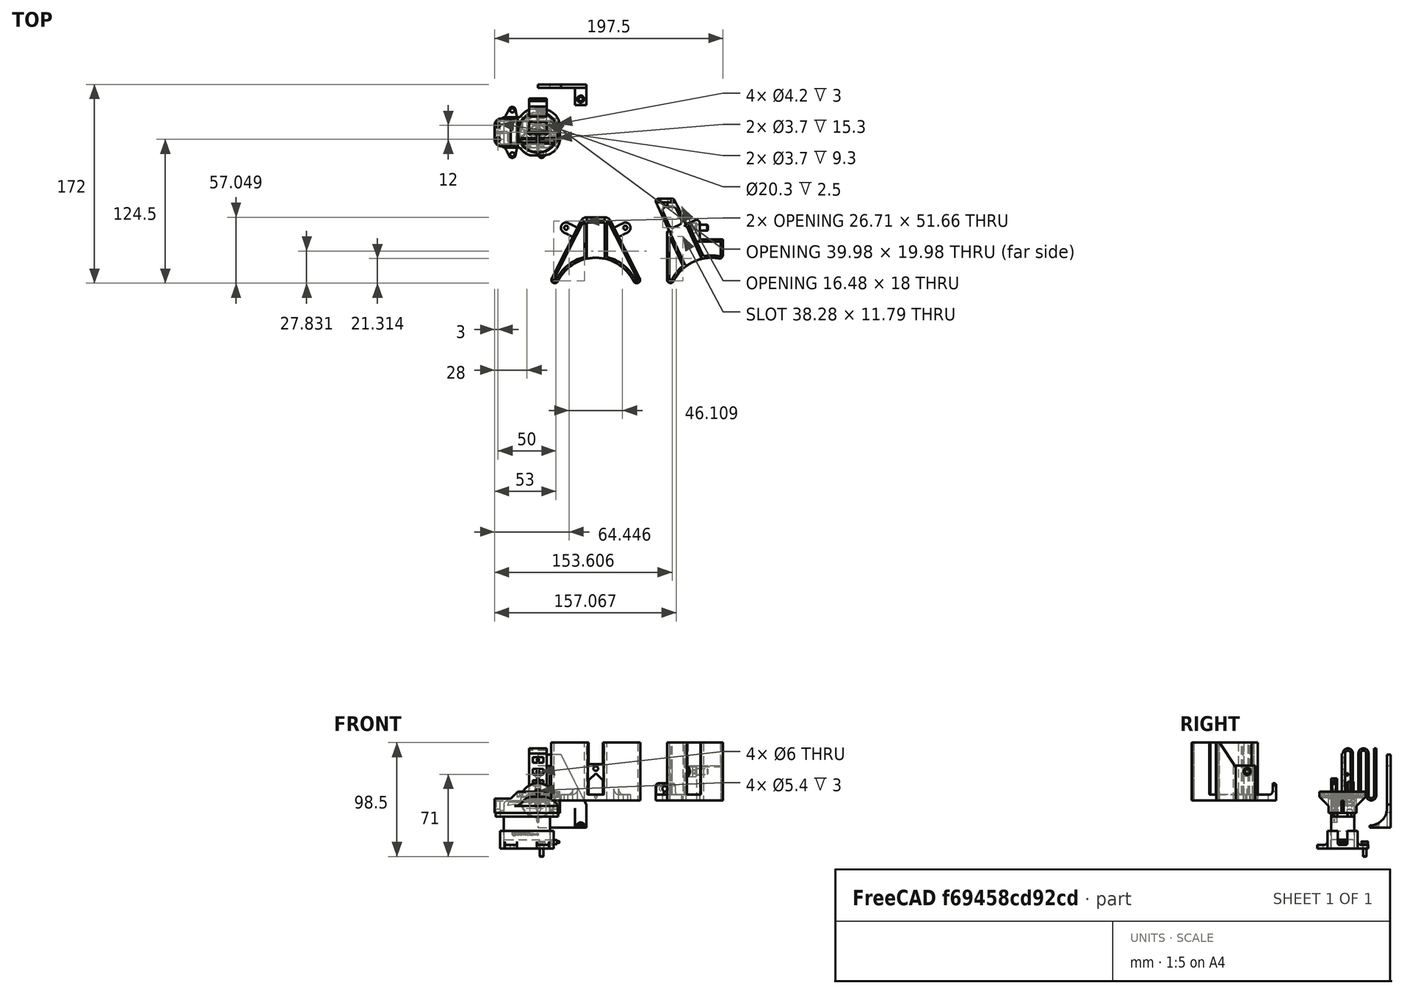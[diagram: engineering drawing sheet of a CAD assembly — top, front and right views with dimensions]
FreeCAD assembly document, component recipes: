
FREECAD ASSEMBLY — COMPONENT RECIPES ("OuterCanMover")

This assembly document has 7 components, labeled P0..P6 below (a component is one placed body or linked part). 7 of them carry a construction recipe — the FreeCAD feature program that regenerates the part from scratch, quoted from this document or its linked companion documents; the rest are supplied as boundary geometry only. No exploded tour is included for this assembly.
COMPONENT P0 — recipe-attached ("aimant", modeled in this document).
Construction recipe (the document's own serialized feature program — sketch geometry with constraints, then the solid features built on it; lengths are millimeters unless a unit is written):

FEATURE [Sketcher::SketchObject] Sketch004
  ArcFitTolerance = 1e-06
  AttachmentSupport = -> [XY_Plane003]
  FullyConstrained = true
  MakeInternals = false
  MapMode = 5
  sketch-geometry (4):
    g0: LineSegment StartX=4.5 StartY=-2.25 StartZ=0 EndX=4.5 EndY=2.25 EndZ=0
    g1: LineSegment StartX=4.5 StartY=2.25 StartZ=0 EndX=-4.5 EndY=2.25 EndZ=0
    g2: LineSegment StartX=-4.5 StartY=2.25 StartZ=0 EndX=-4.5 EndY=-2.25 EndZ=0
    g3: LineSegment StartX=-4.5 StartY=-2.25 StartZ=0 EndX=4.5 EndY=-2.25 EndZ=0
  constraints (11):
    c: Coincident(g0,g1)
    c: Coincident(g1,g2)
    c: Coincident(g2,g3)
    c: Coincident(g3,g0)
    c: Vertical(g0)
    c: Vertical(g2)
    c: Horizontal(g1)
    c: Horizontal(g3)
    c: Symmetric(g1,g0,g-1)
    c: DistanceX(g1,g1) = 9
    c: Distance(g2,g2) = 4.5
FEATURE [PartDesign::Pad] Pad002
  Direction = (0,0,1)
  Length = 2.5
  Length2 = 10
  Profile = -> Sketch004
  ReferenceAxis = -> Sketch004 [N_Axis]
  Suppressed = false
  Type = 0
FEATURE [PartDesign::Body] Body002  label="aimant"
  AllowCompound = false
  Group = -> [Sketch004,Pad002]
  Origin = -> Origin003
  Tip = -> Pad002
COMPONENT P1 — recipe-attached ("aimant002", modeled in this document).
Construction recipe (the document's own serialized feature program — sketch geometry with constraints, then the solid features built on it; lengths are millimeters unless a unit is written):

FEATURE [Sketcher::SketchObject] Sketch032
  ArcFitTolerance = 1e-06
  AttachmentSupport = -> [XY_Plane014]
  FullyConstrained = true
  MakeInternals = false
  MapMode = 5
  sketch-geometry (4):
    g0: LineSegment StartX=4.5 StartY=-2.25 StartZ=0 EndX=4.5 EndY=2.25 EndZ=0
    g1: LineSegment StartX=4.5 StartY=2.25 StartZ=0 EndX=-4.5 EndY=2.25 EndZ=0
    g2: LineSegment StartX=-4.5 StartY=2.25 StartZ=0 EndX=-4.5 EndY=-2.25 EndZ=0
    g3: LineSegment StartX=-4.5 StartY=-2.25 StartZ=0 EndX=4.5 EndY=-2.25 EndZ=0
  constraints (11):
    c: Coincident(g0,g1)
    c: Coincident(g1,g2)
    c: Coincident(g2,g3)
    c: Coincident(g3,g0)
    c: Vertical(g0)
    c: Vertical(g2)
    c: Horizontal(g1)
    c: Horizontal(g3)
    c: Symmetric(g1,g0,g-1)
    c: DistanceX(g1,g1) = 9
    c: Distance(g2,g2) = 4.5
FEATURE [PartDesign::Pad] Pad014
  Direction = (0,0,1)
  Length = 2.5
  Length2 = 10
  Profile = -> Sketch032
  ReferenceAxis = -> Sketch032 [N_Axis]
  Suppressed = false
  Type = 0
FEATURE [PartDesign::Body] Body008  label="aimant002"
  AllowCompound = false
  Group = -> [Sketch032,Pad014]
  Origin = -> Origin014
  Tip = -> Pad014
COMPONENT P2 — recipe-attached ("OuterCanMover_G", modeled in this document).
Construction recipe (the document's own serialized feature program — sketch geometry with constraints, then the solid features built on it; lengths are millimeters unless a unit is written):

FEATURE [Sketcher::SketchObject] Sketch
  ArcFitTolerance = 1e-06
  AttachmentSupport = -> [XY_Plane]
  FullyConstrained = true
  MakeInternals = false
  MapMode = 5
  sketch-geometry (18):
    g0: Circle [constr] CenterX=0 CenterY=-62.5 CenterZ=0 NormalX=0 NormalY=0 NormalZ=1 AngleXU=0 Radius=36.25
    g1: LineSegment [constr] StartX=-10 StartY=10 StartZ=0 EndX=-10 EndY=-10 EndZ=0
    g2: LineSegment [constr] StartX=-10 StartY=-10 StartZ=0 EndX=10 EndY=-10 EndZ=0
    g3: LineSegment [constr] StartX=10 StartY=-10 StartZ=0 EndX=10 EndY=10 EndZ=0
    g4: LineSegment [constr] StartX=10 StartY=10 StartZ=0 EndX=-10 EndY=10 EndZ=0
    g5: ArcOfCircle CenterX=0 CenterY=-62.5 CenterZ=0 NormalX=0 NormalY=0 NormalZ=1 AngleXU=0 Radius=36.5 StartAngle=1.39264 EndAngle=2.6779
    g6: LineSegment StartX=10 StartY=-10 StartZ=0 EndX=-10 EndY=-10 EndZ=0
    g7: LineSegment StartX=-10 StartY=-10 StartZ=0 EndX=-10 EndY=10 EndZ=0
    g8: LineSegment StartX=-14 StartY=14 StartZ=0 EndX=-23.3291 EndY=14 EndZ=0
    g9: LineSegment StartX=-38.3291 StartY=-1 StartZ=0 EndX=-38.3291 EndY=-44.8335 EndZ=0
    g10: ArcOfCircle CenterX=-14 CenterY=10 CenterZ=0 NormalX=0 NormalY=0 NormalZ=1 AngleXU=0 Radius=4 StartAngle=0 EndAngle=1.5708
    g11: GeomPoint [constr] X=-10 Y=14 Z=0
    g12: LineSegment StartX=10 StartY=-10 StartZ=0 EndX=10 EndY=-23.6252 EndZ=0
    g13: ArcOfCircle CenterX=-35.3291 CenterY=-44.8335 CenterZ=0 NormalX=0 NormalY=0 NormalZ=1 AngleXU=0 Radius=3 StartAngle=3.14159 EndAngle=5.81949
    g14: ArcOfCircle CenterX=7 CenterY=-23.6252 CenterZ=0 NormalX=0 NormalY=0 NormalZ=1 AngleXU=0 Radius=3 StartAngle=4.53423 EndAngle=6.28319
    g15: LineSegment [constr] StartX=-38.3291 StartY=14 StartZ=0 EndX=-16.3503 EndY=-29.8669 EndZ=0
    g16: ArcOfCircle CenterX=-23.3291 CenterY=-1 CenterZ=0 NormalX=0 NormalY=0 NormalZ=1 AngleXU=0 Radius=15 StartAngle=1.5708 EndAngle=3.14159
    g17: GeomPoint [constr] X=-38.3291 Y=14 Z=0
  constraints (44):
    c: Coincident(g1,g2)
    c: Coincident(g2,g3)
    c: Coincident(g3,g4)
    c: Vertical(g1)
    c: Vertical(g3)
    c: Horizontal(g2)
    c: Horizontal(g4)
    c: Symmetric(g1,g2,g-1)
    c: Equal(g4,g3)
    c: Coincident(g5,g0)
    c: DistanceY(g3,g3) = 20
    c: Diameter(g0) = 72.5
    c: Coincident(g7,g6)
    c: Vertical(g7)
    c: Horizontal(g8)
    c: Vertical(g9)
    c: Coincident(g1,g4)
    c: Distance(g11,g1) = 4
    c: PointOnObject(g11,g7)
    c: PointOnObject(g11,g8)
    c: Tangent(g7,g10) = -1.5708
    c: Tangent(g8,g10) = -1.5708
    c: Radius(g10) = 4
    c: PointOnObject(g0,g-2)
    c: DistanceY(g0,g-1) = 62.5
    c: Coincident(g12,g6)
    c: Vertical(g12)
    c: Coincident(g1,g6)
    c: Tangent(g9,g13) = -1.5708
    c: Tangent(g5,g13) = 1.5708
    c: Tangent(g5,g14) = 1.5708
    c: Tangent(g12,g14) = 1.5708
    c: Equal(g14,g13)
    c: Radius(g13) = 3
    c: Coincident(g15,g17)
    c: PointOnObject(g15,g5)
    c: Symmetric(g14,g13,g15)
    c: Coincident(g6,g2)
    c: PointOnObject(g17,g8)
    c: PointOnObject(g17,g9)
    c: Tangent(g8,g16) = -1.5708
    c: Tangent(g9,g16) = -1.5708
    c: Radius(g16) = 15
    c: Diameter(g5) = 73
FEATURE [PartDesign::Pad] Pad
  Direction = (0,0,1)
  Length = 50
  Length2 = 10
  Profile = -> Sketch
  ReferenceAxis = -> Sketch [N_Axis]
  Suppressed = false
  Type = 0
FEATURE [Sketcher::SketchObject] Sketch001
  ArcFitTolerance = 1e-06
  AttachmentOffset = pos=(0,0,5) rot=(0,0,1;0rad)
  AttachmentSupport = -> [XY_Plane]
  ExternalGeometry = -> [Pad]
  FullyConstrained = true
  MakeInternals = false
  MapMode = 5
  Placement = pos=(0,0,5) rot=(0,0,1;0rad)
  sketch-geometry (25):
    g0: LineSegment [constr] StartX=-44.1685 StartY=14 StartZ=0 EndX=-35.9616 EndY=-3.59975 EndZ=0
    g1: LineSegment StartX=-8.60751 StartY=-25.8214 StartZ=0 EndX=-21.3706 EndY=1.54911 EndZ=0
    g2: LineSegment StartX=-44.1685 StartY=14 StartZ=0 EndX=-27.1765 EndY=14 EndZ=0
    g3: ArcOfCircle CenterX=0 CenterY=-62.5 CenterZ=0 NormalX=0 NormalY=0 NormalZ=1 AngleXU=0 Radius=36.5 StartAngle=1.82252 EndAngle=2.19174
    g4: LineSegment [constr] StartX=0 StartY=-62.5 StartZ=0 EndX=-35.6725 EndY=14 EndZ=0
    g5: LineSegment StartX=-22.5646 StartY=-32.3297 StartZ=0 EndX=-21.6583 EndY=-31.9071 EndZ=0
    g6: LineSegment StartX=-8.60751 StartY=-25.8214 StartZ=0 EndX=-9.51381 EndY=-26.244 EndZ=0
    g7: LineSegment StartX=-21.6583 StartY=-31.9071 StartZ=0 EndX=-21.2357 EndY=-32.8134 EndZ=0
    g8: LineSegment StartX=-9.51381 StartY=-26.244 StartZ=0 EndX=-9.0912 EndY=-27.1503 EndZ=0
    g9: LineSegment [constr] StartX=-22.5646 StartY=-32.3297 StartZ=0 EndX=-8.60751 EndY=-25.8214 EndZ=0
    g10: LineSegment StartX=-35.9616 StartY=-3.59975 StartZ=0 EndX=-34.6022 EndY=-2.96583 EndZ=0
    g11: LineSegment StartX=-21.3706 StartY=1.54911 StartZ=0 EndX=-22.73 EndY=0.915178 EndZ=0
    g12: LineSegment StartX=-34.6022 StartY=-2.96583 StartZ=0 EndX=-33.9683 EndY=-4.32529 EndZ=0
    g13: LineSegment StartX=-23.364 StartY=2.27464 StartZ=0 EndX=-22.73 EndY=0.915178 EndZ=0
    g14: LineSegment StartX=-35.3277 StartY=-4.95922 StartZ=0 EndX=-22.5646 EndY=-32.3297 EndZ=0
    g15: LineSegment [constr] StartX=-22.0045 StartY=2.90857 StartZ=0 EndX=-27.1765 EndY=14 EndZ=0
    g16: LineSegment StartX=-23.364 StartY=2.27464 StartZ=0 EndX=-22.0045 EndY=2.90857 EndZ=0
    g17: LineSegment StartX=-33.9683 StartY=-4.32529 StartZ=0 EndX=-35.3277 EndY=-4.95922 EndZ=0
    g18: LineSegment [constr] StartX=-35.9616 StartY=-3.59975 StartZ=0 EndX=-35.3277 EndY=-4.95922 EndZ=0
    g19: LineSegment [constr] StartX=-22.0045 StartY=2.90857 StartZ=0 EndX=-21.3706 EndY=1.54911 EndZ=0
    g20: ArcOfCircle CenterX=-20.8978 CenterY=10 CenterZ=0 NormalX=0 NormalY=0 NormalZ=1 AngleXU=0 Radius=4 StartAngle=1.5708 EndAngle=3.57792
    g21: LineSegment StartX=-38.3291 StartY=-4.12459 StartZ=0 EndX=-44.1685 EndY=14 EndZ=0
    g22: LineSegment StartX=-24.523 StartY=8.30953 StartZ=0 EndX=-22.0045 EndY=2.90857 EndZ=0
    g23: LineSegment StartX=-27.1765 StartY=14 StartZ=0 EndX=-20.8978 EndY=14 EndZ=0
    g24: ArcOfCircle CenterX=-37.0872 CenterY=-4.12459 CenterZ=0 NormalX=0 NormalY=0 NormalZ=1 AngleXU=0 Radius=1.2419 StartAngle=0.436322 EndAngle=3.14159
  constraints (64):
    c: PointOnObject(g15,g-3)
    c: Coincident(g2,g15)
    c: Parallel(g1,g0)
    c: Coincident(g3,g-5)
    c: Angle(g-2,g1) = 0.436332
    c: Coincident(g4,g3)
    c: Parallel(g4,g1)
    c: Coincident(g2,g0)
    c: Horizontal(g2)
    c: Symmetric(g0,g15,g4)
    c: Coincident(g7,g5)
    c: Coincident(g8,g6)
    c: Coincident(g3,g8)
    c: Symmetric(g6,g5,g4)
    c: Coincident(g9,g5)
    c: Coincident(g9,g6)
    c: PointOnObject(g6,g9)
    c: PointOnObject(g5,g9)
    c: Perpendicular(g5,g7)
    c: Perpendicular(g6,g8)
    c: Coincident(g3,g7)
    c: PointOnObject(g3,g-5)
    c: Distance(g7,g7) = 1
    c: Distance(g5,g5) = 1
    c: Coincident(g14,g5)
    c: Coincident(g1,g6)
    c: Distance(g1,g14) = 15.4
    c: PointOnObject(g16,g15)
    c: Distance(g17,g10) = 1.5
    c: Symmetric(g12,g13,g4)
    c: Perpendicular(g0,g10) = 1.5708
    c: PointOnObject(g14,g11)
    c: Perpendicular(g1,g11) = 1.5708
    c: PointOnObject(g15,g16)
    c: Coincident(g11,g13)
    c: Coincident(g17,g12)
    c: Perpendicular(g10,g12) = 4.71239
    c: Perpendicular(g12,g17)
    c: Perpendicular(g15,g16)
    c: Parallel(g15,g1)
    c: Coincident(g18,g0)
    c: Coincident(g18,g17)
    c: Coincident(g19,g15)
    c: Coincident(g19,g1)
    c: Parallel(g19,g15)
    c: Coincident(g13,g16)
    c: Parallel(g18,g0)
    c: Coincident(g14,g17)
    c: Equal(g11,g17)
    c: Distance(g14,g5) = 30.2
    c: Parallel(g1,g14)
    c: Distance(g10,g10) = 1.5
    c: PointOnObject(g20,g15)
    c: PointOnObject(g20,g-3)
    c: Coincident(g21,g0)
    c: Coincident(g22,g16)
    c: Coincident(g23,g2)
    c: Tangent(g22,g20) = -1.5708
    c: Tangent(g23,g20) = 1.5708
    c: Radius(g20) = 4
    c: Tangent(g24,g-4) = -1.5708
    c: Coincident(g21,g24)
    c: Coincident(g24,g0)
    c: Tangent(g24,g18)
FEATURE [PartDesign::Pocket] Pocket
  BaseFeature = -> Pad
  Direction = (0,0,-1)
  Length = 5
  Length2 = 5
  Profile = -> Sketch001
  ReferenceAxis = -> Sketch001 [N_Axis]
  Reversed = true
  Suppressed = false
  Type = 1
FEATURE [Sketcher::SketchObject] Sketch007
  ArcFitTolerance = 1e-06
  AttachmentSupport = -> [Pocket]
  FullyConstrained = true
  MakeInternals = false
  MapMode = 5
  Placement = pos=(-10,0,0) rot=(0.57735,0.57735,0.57735;2.0944rad)
  sketch-geometry (1):
    g0: Circle CenterX=0 CenterY=25 CenterZ=0 NormalX=0 NormalY=0 NormalZ=1 AngleXU=0 Radius=3
  constraints (3):
    c: PointOnObject(g0,g-2)
    c: Diameter(g0) = 6
    c: DistanceY(g-1,g0) = 25
FEATURE [PartDesign::Pocket] Pocket004  label="vis1"
  BaseFeature = -> Pocket
  Direction = (-1,0,0)
  Length = 12
  Length2 = 5
  Profile = -> Sketch007
  ReferenceAxis = -> Sketch007 [N_Axis]
  Suppressed = false
  Type = 0
FEATURE [Sketcher::SketchObject] Sketch008
  ArcFitTolerance = 1e-06
  AttachmentOffset = pos=(0,0,-3) rot=(0,0,1;0rad)
  AttachmentSupport = -> [Pocket004]
  FullyConstrained = true
  MakeInternals = false
  MapMode = 5
  Placement = pos=(-13,0,0) rot=(0.57735,0.57735,0.57735;2.0944rad)
  sketch-geometry (1):
    g0: Circle CenterX=0 CenterY=25 CenterZ=0 NormalX=0 NormalY=0 NormalZ=1 AngleXU=0 Radius=4.25
  constraints (3):
    c: Diameter(g0) = 8.5
    c: PointOnObject(g0,g-2)
    c: DistanceY(g-1,g0) = 25
FEATURE [PartDesign::Pocket] Pocket005  label="vis2"
  BaseFeature = -> Pocket004
  Direction = (-1,0,0)
  Length = 5
  Length2 = 5
  Profile = -> Sketch008
  ReferenceAxis = -> Sketch008 [N_Axis]
  Suppressed = false
  Type = 1
FEATURE [Sketcher::SketchObject] Sketch009
  ArcFitTolerance = 1e-06
  AttachmentSupport = -> [Pocket005]
  ExternalGeometry = -> [Pocket005]
  FullyConstrained = true
  MakeInternals = false
  MapMode = 5
  Placement = pos=(0,0,50) rot=(0,0,1;0rad)
  sketch-geometry (14):
    g0: LineSegment StartX=-36.3291 StartY=-7.54414 StartZ=0 EndX=-36.3291 EndY=-44.8335 EndZ=0
    g1: LineSegment StartX=-36.3291 StartY=-7.54414 StartZ=0 EndX=-24.5371 EndY=-32.8322 EndZ=0
    g2: ArcOfCircle CenterX=0 CenterY=-62.5 CenterZ=0 NormalX=0 NormalY=0 NormalZ=1 AngleXU=0 Radius=38.5 StartAngle=2.26182 EndAngle=2.6779
    g3: ArcOfCircle CenterX=-35.3291 CenterY=-44.8335 CenterZ=0 NormalX=0 NormalY=0 NormalZ=1 AngleXU=0 Radius=1 StartAngle=3.14159 EndAngle=5.81949
    g4: LineSegment StartX=-36.8069 StartY=-1.78714 StartZ=0 EndX=-22.8497 EndY=4.72118 EndZ=0
    g5: LineSegment StartX=-22.8497 StartY=4.72118 StartZ=0 EndX=-22.0045 EndY=2.90857 EndZ=0
    g6: LineSegment StartX=-22.0045 StartY=2.90857 StartZ=0 EndX=-35.9616 EndY=-3.59975 EndZ=0
    g7: LineSegment StartX=-35.9616 StartY=-3.59975 StartZ=0 EndX=-36.8069 EndY=-1.78714 EndZ=0
    g8: LineSegment [constr] StartX=-35.9616 StartY=-3.59975 StartZ=0 EndX=-37.7743 EndY=-4.44499 EndZ=0
    g9: ArcOfCircle CenterX=0 CenterY=-62.5 CenterZ=0 NormalX=0 NormalY=0 NormalZ=1 AngleXU=0 Radius=38.5 StartAngle=1.39264 EndAngle=1.75244
    g10: LineSegment StartX=-12.8458 StartY=-12 StartZ=0 EndX=-6.95473 EndY=-24.6334 EndZ=0
    g11: LineSegment StartX=8 StartY=-23.6252 StartZ=0 EndX=8 EndY=-12 EndZ=0
    g12: LineSegment StartX=8 StartY=-12 StartZ=0 EndX=-12.8458 EndY=-12 EndZ=0
    g13: ArcOfCircle CenterX=7 CenterY=-23.6252 CenterZ=0 NormalX=0 NormalY=0 NormalZ=1 AngleXU=0 Radius=1 StartAngle=4.53423 EndAngle=6.28319
  constraints (36):
    c: Vertical(g0)
    c: Coincident(g2,g1)
    c: Tangent(g3,g2) = 1.5708
    c: Tangent(g3,g0) = -1.5708
    c: Coincident(g5,g4)
    c: Coincident(g6,g5)
    c: Coincident(g7,g6)
    c: Coincident(g7,g4)
    c: Perpendicular(g4,g7)
    c: Perpendicular(g7,g6)
    c: Perpendicular(g5,g6)
    c: Coincident(g6,g-4)
    c: Coincident(g5,g-3)
    c: Coincident(g-6,g3)
    c: Perpendicular(g6,g1)
    c: Coincident(g1,g0)
    c: Distance(g0,g-6) = 2
    c: Coincident(g8,g6)
    c: Parallel(g8,g6)
    c: PointOnObject(g8,g1)
    c: Distance(g8,g8) = 2
    c: Coincident(g2,g-5)
    c: Coincident(g9,g2)
    c: Coincident(g11,g12)
    c: Coincident(g12,g10)
    c: Vertical(g11)
    c: Horizontal(g12)
    c: Coincident(g9,g10)
    c: Tangent(g9,g13) = 1.5708
    c: Tangent(g11,g13) = -1.5708
    c: Parallel(g10,g1)
    c: Coincident(g13,g-9)
    c: Distance(g11,g-9) = 2
    c: DistanceY(g11,g-8) = 2
    c: Distance(g10,g-10) = 2
    c: Distance(g5,g5) = 2
FEATURE [PartDesign::Pocket] Pocket006
  BaseFeature = -> Pocket005
  Direction = (0,0,-1)
  Length = 5
  Length2 = 5
  Profile = -> Sketch009
  ReferenceAxis = -> Sketch009 [N_Axis]
  Suppressed = false
  Type = 1
FEATURE [PartDesign::Pocket] Pocket007
  BaseFeature = -> Pocket006
  Direction = (0,0,-1)
  Length = 5
  Length2 = 5
  Profile = -> Pocket006 [Face48]
  Suppressed = false
  Type = 0
FEATURE [Sketcher::SketchObject] Sketch011
  ArcFitTolerance = 1e-06
  AttachmentSupport = -> [Pocket007]
  ExternalGeometry = -> [Pocket007,Sketch009]
  FullyConstrained = true
  MakeInternals = false
  MapMode = 5
  Placement = pos=(0,0,50) rot=(0,0,1;0rad)
  sketch-geometry (10):
    g0: ArcOfCircle CenterX=-20.8978 CenterY=10 CenterZ=0 NormalX=0 NormalY=0 NormalZ=1 AngleXU=0 Radius=4 StartAngle=1.5708 EndAngle=3.57792
    g1: ArcOfCircle CenterX=-14 CenterY=10 CenterZ=0 NormalX=0 NormalY=0 NormalZ=1 AngleXU=0 Radius=4 StartAngle=0 EndAngle=1.5708
    g2: LineSegment StartX=-24.523 StartY=8.30953 StartZ=0 EndX=-22.0045 EndY=2.90857 EndZ=0
    g3: LineSegment StartX=-10 StartY=-10 StartZ=0 EndX=-10 EndY=10 EndZ=0
    g4: LineSegment StartX=-14 StartY=14 StartZ=0 EndX=-20.8978 EndY=14 EndZ=0
    g5: LineSegment StartX=-22.0045 StartY=2.90857 StartZ=0 EndX=-20.1919 EndY=3.7538 EndZ=0
    g6: LineSegment StartX=-20.1919 StartY=3.7538 StartZ=0 EndX=-12.8458 EndY=-12 EndZ=0
    g7: LineSegment StartX=8 StartY=-10 StartZ=0 EndX=-10 EndY=-10 EndZ=0
    g8: LineSegment StartX=-12.8458 StartY=-12 StartZ=0 EndX=8 EndY=-12 EndZ=0
    g9: LineSegment StartX=8 StartY=-12 StartZ=0 EndX=8 EndY=-10 EndZ=0
  constraints (22):
    c: Coincident(g0,g-6)
    c: Coincident(g1,g-5)
    c: Tangent(g4,g0) = -1.5708
    c: Tangent(g4,g1) = -1.5708
    c: Tangent(g3,g1) = -1.5708
    c: Tangent(g2,g0) = -1.5708
    c: Coincident(g0,g-6)
    c: Coincident(g5,g2)
    c: Coincident(g6,g5)
    c: Perpendicular(g2,g5)
    c: Perpendicular(g5,g6)
    c: Coincident(g2,g-9)
    c: Coincident(g6,g-7)
    c: Coincident(g8,g9)
    c: Coincident(g9,g7)
    c: Horizontal(g7)
    c: Horizontal(g8)
    c: Vertical(g9)
    c: Coincident(g8,g6)
    c: Coincident(g7,g3)
    c: Coincident(g3,g-4)
    c: DistanceX(g7,g7) = 18
FEATURE [PartDesign::Pocket] Pocket008
  BaseFeature = -> Pocket007
  Direction = (0,0,-1)
  Length = 20
  Length2 = 5
  Profile = -> Sketch011
  ReferenceAxis = -> Sketch011 [N_Axis]
  Suppressed = false
  Type = 0
FEATURE [Sketcher::SketchObject] Sketch012
  ArcFitTolerance = 1e-06
  AttachmentSupport = -> [Pocket008]
  ExternalGeometry = -> [Pocket008,Sketch009]
  FullyConstrained = true
  MakeInternals = false
  MapMode = 5
  Placement = pos=(0,0,30) rot=(0,0,1;0rad)
  sketch-geometry (4):
    g0: LineSegment StartX=-27.1765 StartY=14 StartZ=0 EndX=-22.0045 EndY=2.90857 EndZ=0
    g1: LineSegment StartX=-22.0045 StartY=2.90857 StartZ=0 EndX=-10 EndY=8.50636 EndZ=0
    g2: LineSegment StartX=-10 StartY=8.50636 StartZ=0 EndX=-10 EndY=14 EndZ=0
    g3: LineSegment StartX=-10 StartY=14 StartZ=0 EndX=-27.1765 EndY=14 EndZ=0
  constraints (11):
    c: Coincident(g0,g1)
    c: Coincident(g1,g2)
    c: Coincident(g2,g3)
    c: Coincident(g3,g0)
    c: Vertical(g2)
    c: Horizontal(g3)
    c: Coincident(g0,g-4)
    c: Perpendicular(g0,g1)
    c: PointOnObject(g-3,g0)
    c: PointOnObject(g-5,g3)
    c: PointOnObject(g-6,g2)
FEATURE [PartDesign::Pocket] Pocket009
  BaseFeature = -> Pocket008
  Direction = (0,0,-1)
  Length = 5
  Length2 = 5
  Profile = -> Sketch012
  ReferenceAxis = -> Sketch012 [N_Axis]
  Suppressed = false
  Type = 1
FEATURE [PartDesign::Fillet] Fillet
  Base = -> Pocket009 [Edge83]
  BaseFeature = -> Pocket009
  Radius = 3
  SupportTransform = false
  Suppressed = false
  UseAllEdges = false
FEATURE [PartDesign::Chamfer] Chamfer
  Angle = 45
  Base = -> Fillet [Edge42]
  BaseFeature = -> Fillet
  ChamferType = 1
  FlipDirection = false
  Size = 21
  Size2 = 14
  SupportTransform = false
  Suppressed = false
  UseAllEdges = false
FEATURE [PartDesign::Pad] Pad006
  BaseFeature = -> Chamfer
  Direction = (-0.422618,0.906308,0)
  Length = 40
  Length2 = 10
  Profile = -> Chamfer [Face15]
  Suppressed = false
  Type = 0
FEATURE [Sketcher::SketchObject] Sketch017
  ArcFitTolerance = 1e-06
  AttachmentOffset = pos=(0,0,25) rot=(0,0,1;0rad)
  AttachmentSupport = -> [XZ_Plane]
  ExternalGeometry = -> [Pad006]
  FullyConstrained = true
  MakeInternals = false
  MapMode = 5
  Placement = pos=(0,25,-5.6e-15) rot=(0,0.707107,0.707107;3.14159rad)
  sketch-geometry (4):
    g0: LineSegment StartX=22.8664 StartY=5 StartZ=0 EndX=22.8664 EndY=7.1e-15 EndZ=0
    g1: LineSegment StartX=22.8664 StartY=7.1e-15 StartZ=0 EndX=52.8664 EndY=7.1e-15 EndZ=0
    g2: LineSegment StartX=52.8664 StartY=7.1e-15 StartZ=0 EndX=52.8664 EndY=5 EndZ=0
    g3: LineSegment StartX=52.8664 StartY=5 StartZ=0 EndX=22.8664 EndY=5 EndZ=0
  constraints (10):
    c: Coincident(g0,g1)
    c: Coincident(g1,g2)
    c: Coincident(g2,g3)
    c: Coincident(g3,g0)
    c: Vertical(g0)
    c: Horizontal(g1)
    c: Horizontal(g3)
    c: Coincident(g1,g-3)
    c: Coincident(g2,g-3)
    c: DistanceX(g3,g3) = 30
FEATURE [PartDesign::Pocket] Pocket012
  BaseFeature = -> Pad006
  Direction = (0,-1,2e-16)
  Length = 5
  Length2 = 5
  Profile = -> Sketch017
  ReferenceAxis = -> Sketch017 [N_Axis]
  Reversed = true
  Suppressed = false
  Type = 0
FEATURE [Sketcher::SketchObject] Sketch018
  ArcFitTolerance = 1e-06
  AttachmentOffset = pos=(0,0,5) rot=(0,0,1;0rad)
  AttachmentSupport = -> [XY_Plane]
  ExternalGeometry = -> [Pocket012]
  FullyConstrained = true
  MakeInternals = false
  MapMode = 5
  Placement = pos=(0,0,5) rot=(0,0,1;0rad)
  sketch-geometry (4):
    g0: LineSegment StartX=-49.2979 StartY=25 StartZ=0 EndX=-47.899 EndY=22 EndZ=0
    g1: LineSegment StartX=-49.2979 StartY=25 StartZ=0 EndX=-32.3059 EndY=25 EndZ=0
    g2: LineSegment StartX=-32.3059 StartY=25 StartZ=0 EndX=-30.907 EndY=22 EndZ=0
    g3: LineSegment StartX=-30.907 StartY=22 StartZ=0 EndX=-47.899 EndY=22 EndZ=0
  constraints (10):
    c: Coincident(g0,g-5)
    c: PointOnObject(g0,g-5)
    c: Coincident(g1,g0)
    c: Coincident(g1,g-4)
    c: Coincident(g2,g1)
    c: Coincident(g3,g2)
    c: Coincident(g3,g0)
    c: Parallel(g3,g1)
    c: Parallel(g2,g0)
    c: DistanceY(g2,g2) = 3
FEATURE [PartDesign::Pad] Pad007
  BaseFeature = -> Pocket012
  Direction = (0,0,1)
  Length = 10
  Length2 = 10
  Profile = -> Sketch018
  ReferenceAxis = -> Sketch018 [N_Axis]
  Suppressed = false
  Type = 0
FEATURE [Sketcher::SketchObject] Sketch019
  ArcFitTolerance = 1e-06
  AttachmentOffset = pos=(-40,10,-23) rot=(0,1,0;0.436332rad)
  AttachmentSupport = -> [XZ_Plane]
  FullyConstrained = false
  MakeInternals = false
  MapMode = 5
  Placement = pos=(-40,23,10) rot=(0.954201,0.211541,0.211541;1.61766rad)
  sketch-geometry (2):
    g0: Circle CenterX=0 CenterY=0 CenterZ=0 NormalX=0 NormalY=0 NormalZ=1 AngleXU=0 Radius=2.5
    g1: LineSegment [constr] StartX=-9 StartY=3.11249 StartZ=0 EndX=-9 EndY=-2.45643 EndZ=0
  constraints (4):
    c: Coincident(g0,g-1)
    c: Diameter(g0) = 5
    c: Vertical(g1)
    c: Distance(g1,g-2) = 9
FEATURE [PartDesign::Groove] Groove
  Angle = 360
  Angle2 = 60
  Axis = (0,-1e-15,-5.56892)
  Base = (-48.1568,19.1964,13.1125)
  BaseFeature = -> Pad007
  Profile = -> Sketch019
  ReferenceAxis = -> Sketch019 [Axis]
  Reversed = true
  Suppressed = false
  Type = 0
FEATURE [Sketcher::SketchObject] Sketch020
  ArcFitTolerance = 1e-06
  AttachmentOffset = pos=(0,0,0) rot=(0,0,1;0.436332rad)
  AttachmentSupport = -> [Groove]
  ExternalGeometry = -> [Groove]
  FullyConstrained = true
  MakeInternals = false
  MapMode = 5
  Placement = pos=(0,0,5) rot=(0,0,1;0.436332rad)
  sketch-geometry (8):
    g0: ArcOfCircle CenterX=-29.1136 CenterY=30.1818 CenterZ=0 NormalX=0 NormalY=0 NormalZ=1 AngleXU=0 Radius=3 StartAngle=1.13446 EndAngle=3.14159
    g1: ArcOfCircle CenterX=-23.7136 CenterY=27.6637 CenterZ=0 NormalX=0 NormalY=0 NormalZ=1 AngleXU=0 Radius=3 StartAngle=0 EndAngle=1.13446
    g2: ArcOfCircle CenterX=-29.1136 CenterY=16.9356 CenterZ=0 NormalX=0 NormalY=0 NormalZ=1 AngleXU=0 Radius=3 StartAngle=3.14159 EndAngle=4.71239
    g3: ArcOfCircle CenterX=-23.7136 CenterY=16.9356 CenterZ=0 NormalX=0 NormalY=0 NormalZ=1 AngleXU=0 Radius=3 StartAngle=4.71239 EndAngle=6.28319
    g4: LineSegment StartX=-32.1136 StartY=30.1818 StartZ=0 EndX=-32.1136 EndY=16.9356 EndZ=0
    g5: LineSegment StartX=-29.1136 StartY=13.9356 StartZ=0 EndX=-23.7136 EndY=13.9356 EndZ=0
    g6: LineSegment StartX=-20.7136 StartY=16.9356 StartZ=0 EndX=-20.7136 EndY=27.6637 EndZ=0
    g7: LineSegment StartX=-22.4458 StartY=30.3826 StartZ=0 EndX=-27.8458 EndY=32.9007 EndZ=0
  constraints (20):
    c: Tangent(g7,g0) = -1.5708
    c: Vertical(g4)
    c: Vertical(g6)
    c: Horizontal(g5)
    c: Tangent(g5,g2) = -1.5708
    c: Tangent(g4,g2) = -1.5708
    c: Tangent(g5,g3) = -1.5708
    c: Tangent(g6,g3) = -1.5708
    c: Tangent(g6,g1) = -1.5708
    c: Tangent(g7,g1) = -1.5708
    c: DistanceX(g1,g-4) = 2
    c: Distance(g0,g-3) = 2
    c: Angle(g7,g-1) = 0.436332
    c: Tangent(g4,g0) = -1.5708
    c: Equal(g0,g1)
    c: Equal(g1,g3)
    c: Equal(g3,g2)
    c: Radius(g2) = 3
    c: DistanceY(g-4,g3) = 2
    c: DistanceY(g0,g-3) = 10
FEATURE [PartDesign::Pocket] Pocket013
  BaseFeature = -> Groove
  Direction = (0,0,-1)
  Length = 5
  Length2 = 5
  Profile = -> Sketch020
  ReferenceAxis = -> Sketch020 [N_Axis]
  Suppressed = false
  Type = 0
FEATURE [PartDesign::Fillet] Fillet001
  Base = -> Pocket013 [Edge179,Edge185,Edge188]
  BaseFeature = -> Pocket013
  Radius = 3
  SupportTransform = false
  Suppressed = false
  UseAllEdges = false
FEATURE [PartDesign::Fillet] Fillet002
  Base = -> Fillet001 [Edge36,Edge10]
  BaseFeature = -> Fillet001
  Radius = 2
  SupportTransform = false
  Suppressed = false
  UseAllEdges = false
FEATURE [PartDesign::Body] Body  label="Partie_fixe_d"
  AllowCompound = false
  Group = -> [Sketch,Pad,Sketch001,Pocket,Sketch007,Pocket004,Sketch008,Pocket005,Sketch009,Pocket006,Pocket007,Sketch011,Pocket008,Sketch012,Pocket009,Fillet,Chamfer,Pad006,Sketch017,Pocket012,Sketch018,Pad007,Sketch019,Groove,Sketch020,Pocket013,Fillet001,Fillet002]
  Origin = -> Origin
  Placement = pos=(150,-82.5,0) rot=(0,0,1;0rad)
  Tip = -> Fillet002
COMPONENT P3 — recipe-attached ("InnerCanMover_G", modeled in this document).
Construction recipe (the document's own serialized feature program — sketch geometry with constraints, then the solid features built on it; lengths are millimeters unless a unit is written):

FEATURE [Sketcher::SketchObject] Sketch028
  ArcFitTolerance = 1e-06
  AttachmentSupport = -> [XY_Plane011]
  FullyConstrained = true
  MakeInternals = false
  MapMode = 5
  sketch-geometry (10):
    g0: Circle [constr] CenterX=0 CenterY=-62.5 CenterZ=0 NormalX=0 NormalY=0 NormalZ=1 AngleXU=0 Radius=36.25
    g1: ArcOfCircle CenterX=0 CenterY=-62.5 CenterZ=0 NormalX=0 NormalY=0 NormalZ=1 AngleXU=0 Radius=36.5 StartAngle=0.458985 EndAngle=2.68261
    g2: LineSegment StartX=8.05039 StartY=9 StartZ=0 EndX=-8.05039 EndY=9 EndZ=0
    g3: LineSegment StartX=-12.5 StartY=6.28057 StartZ=0 EndX=-38.0816 EndY=-43.6317 EndZ=0
    g4: ArcOfCircle CenterX=8.05039 CenterY=4 CenterZ=0 NormalX=0 NormalY=0 NormalZ=1 AngleXU=0 Radius=5 StartAngle=0.473623 EndAngle=1.5708
    g5: LineSegment StartX=12.5 StartY=6.28057 StartZ=0 EndX=38.0816 EndY=-43.6317 EndZ=0
    g6: ArcOfCircle CenterX=-35.4119 CenterY=-45 CenterZ=0 NormalX=0 NormalY=0 NormalZ=1 AngleXU=0 Radius=3 StartAngle=2.66797 EndAngle=5.8242
    g7: ArcOfCircle CenterX=35.4119 CenterY=-45 CenterZ=0 NormalX=0 NormalY=0 NormalZ=1 AngleXU=0 Radius=3 StartAngle=3.60058 EndAngle=6.75681
    g8: LineSegment [constr] StartX=-1.8e-15 StartY=9 StartZ=0 EndX=-1.8e-15 EndY=-26 EndZ=0
    g9: ArcOfCircle CenterX=-8.05039 CenterY=4 CenterZ=0 NormalX=0 NormalY=0 NormalZ=1 AngleXU=0 Radius=5 StartAngle=1.5708 EndAngle=2.66797
  constraints (25):
    c: Coincident(g1,g0)
    c: Diameter(g0) = 72.5
    c: Horizontal(g2)
    c: Tangent(g2,g4) = -1.5708
    c: PointOnObject(g0,g-2)
    c: DistanceY(g0,g-1) = 62.5
    c: Tangent(g3,g6) = -1.5708
    c: Tangent(g1,g6) = 1.5708
    c: Tangent(g1,g7) = 1.5708
    c: Tangent(g5,g7) = 1.5708
    c: Equal(g7,g6)
    c: Radius(g6) = 3
    c: PointOnObject(g8,g1)
    c: Symmetric(g7,g6,g8)
    c: Tangent(g2,g9) = -1.5708
    c: Tangent(g3,g9) = -1.5708
    c: Radius(g9) = 5
    c: Diameter(g1) = 73
    c: Tangent(g5,g4) = 1.5708
    c: Equal(g4,g9)
    c: Distance(g3,g4) = 25
    c: DistanceY(g8,g2) = 35
    c: DistanceY(g7,g-1) = 45
    c: Symmetric(g2,g2,g8)
    c: PointOnObject(g8,g2)
FEATURE [PartDesign::Pad] Pad012
  Direction = (0,0,1)
  Length = 50
  Length2 = 10
  Profile = -> Sketch028
  ReferenceAxis = -> Sketch028 [N_Axis]
  Suppressed = false
  Type = 0
FEATURE [Sketcher::SketchObject] Sketch029
  ArcFitTolerance = 1e-06
  AttachmentOffset = pos=(0,0,5) rot=(0,0,1;0rad)
  AttachmentSupport = -> [XY_Plane011]
  ExternalGeometry = -> [Pad012]
  FullyConstrained = true
  MakeInternals = false
  MapMode = 5
  Placement = pos=(0,0,5) rot=(0,0,1;0rad)
  sketch-geometry (22):
    g0: LineSegment [constr] StartX=-7.7 StartY=11.0798 StartZ=0 EndX=-7.7 EndY=6.0798 EndZ=0
    g1: LineSegment StartX=7.7 StartY=-25.6202 StartZ=0 EndX=7.7 EndY=4.5798 EndZ=0
    g2: LineSegment StartX=-7.7 StartY=11.0798 StartZ=0 EndX=7.7 EndY=11.0798 EndZ=0
    g3: ArcOfCircle CenterX=0 CenterY=-62.5 CenterZ=0 NormalX=0 NormalY=0 NormalZ=1 AngleXU=0 Radius=36.5 StartAngle=1.38619 EndAngle=1.7554
    g4: LineSegment [constr] StartX=0 StartY=-62.5 StartZ=0 EndX=0 EndY=11.0798 EndZ=0
    g5: LineSegment StartX=-7.7 StartY=-25.6202 StartZ=0 EndX=-6.7 EndY=-25.6202 EndZ=0
    g6: LineSegment StartX=7.7 StartY=-25.6202 StartZ=0 EndX=6.7 EndY=-25.6202 EndZ=0
    g7: LineSegment StartX=-6.7 StartY=-25.6202 StartZ=0 EndX=-6.7 EndY=-26.6202 EndZ=0
    g8: LineSegment StartX=6.7 StartY=-25.6202 StartZ=0 EndX=6.7 EndY=-26.6202 EndZ=0
    g9: LineSegment [constr] StartX=-7.7 StartY=-25.6202 StartZ=0 EndX=7.7 EndY=-25.6202 EndZ=0
    g10: LineSegment StartX=-7.7 StartY=6.0798 StartZ=0 EndX=-6.2 EndY=6.0798 EndZ=0
    g11: LineSegment StartX=7.7 StartY=4.5798 StartZ=0 EndX=6.2 EndY=4.5798 EndZ=0
    g12: LineSegment StartX=-6.2 StartY=6.0798 StartZ=0 EndX=-6.2 EndY=4.5798 EndZ=0
    g13: LineSegment StartX=6.2 StartY=6.0798 StartZ=0 EndX=6.2 EndY=4.5798 EndZ=0
    g14: LineSegment StartX=-7.7 StartY=4.5798 StartZ=0 EndX=-7.7 EndY=-25.6202 EndZ=0
    g15: LineSegment [constr] StartX=7.7 StartY=6.0798 StartZ=0 EndX=7.7 EndY=11.0798 EndZ=0
    g16: LineSegment StartX=6.2 StartY=6.0798 StartZ=0 EndX=7.7 EndY=6.0798 EndZ=0
    g17: LineSegment StartX=-6.2 StartY=4.5798 StartZ=0 EndX=-7.7 EndY=4.5798 EndZ=0
    g18: LineSegment [constr] StartX=-7.7 StartY=6.0798 StartZ=0 EndX=-7.7 EndY=4.5798 EndZ=0
    g19: LineSegment [constr] StartX=7.7 StartY=6.0798 StartZ=0 EndX=7.7 EndY=4.5798 EndZ=0
    g20: LineSegment StartX=7.7 StartY=11.0798 StartZ=0 EndX=7.7 EndY=6.0798 EndZ=0
    g21: LineSegment StartX=-7.7 StartY=11.0798 StartZ=0 EndX=-7.7 EndY=6.0798 EndZ=0
  constraints (56):
    c: Coincident(g2,g15)
    c: Parallel(g1,g0)
    c: Coincident(g4,g3)
    c: Parallel(g4,g1)
    c: Coincident(g2,g0)
    c: Horizontal(g2)
    c: Symmetric(g0,g15,g4)
    c: Coincident(g7,g5)
    c: Coincident(g8,g6)
    c: Coincident(g3,g8)
    c: Symmetric(g6,g5,g4)
    c: Coincident(g9,g5)
    c: Coincident(g9,g6)
    c: PointOnObject(g6,g9)
    c: PointOnObject(g5,g9)
    c: Perpendicular(g5,g7)
    c: Perpendicular(g6,g8)
    c: Coincident(g3,g7)
    c: Distance(g7,g7) = 1
    c: Distance(g5,g5) = 1
    c: Coincident(g14,g5)
    c: Coincident(g1,g6)
    c: Distance(g1,g14) = 15.4
    c: PointOnObject(g16,g15)
    c: Distance(g17,g10) = 1.5
    c: Symmetric(g12,g13,g4)
    c: Perpendicular(g0,g10) = 1.5708
    c: PointOnObject(g14,g11)
    c: Perpendicular(g1,g11) = 1.5708
    c: PointOnObject(g15,g16)
    c: Coincident(g11,g13)
    c: Coincident(g17,g12)
    c: Perpendicular(g10,g12) = 4.71239
    c: Perpendicular(g12,g17)
    c: Perpendicular(g15,g16)
    c: Parallel(g15,g1)
    c: Coincident(g18,g0)
    c: Coincident(g18,g17)
    c: Coincident(g19,g15)
    c: Coincident(g19,g1)
    c: Parallel(g19,g15)
    c: Coincident(g13,g16)
    c: Parallel(g18,g0)
    c: Coincident(g14,g17)
    c: Equal(g11,g17)
    c: Distance(g14,g5) = 30.2
    c: Parallel(g1,g14)
    c: Distance(g10,g10) = 1.5
    c: Coincident(g20,g16)
    c: Coincident(g2,g20)
    c: Coincident(g21,g0)
    c: Coincident(g21,g0)
    c: Vertical(g21)
    c: PointOnObject(g3,g-3)
    c: Distance(g21,g21) = 5
    c: Coincident(g3,g-3)
FEATURE [PartDesign::Pocket] Pocket018
  BaseFeature = -> Pad012
  Direction = (0,0,-1)
  Length = 5
  Length2 = 5
  Profile = -> Sketch029
  ReferenceAxis = -> Sketch029 [N_Axis]
  Reversed = true
  Suppressed = false
  Type = 1
FEATURE [Sketcher::SketchObject] Sketch040
  ArcFitTolerance = 1e-06
  AttachmentSupport = -> [XY_Plane011]
  ExternalGeometry = -> [Pocket018]
  FullyConstrained = true
  MakeInternals = false
  MapMode = 5
  sketch-geometry (6):
    g0: LineSegment StartX=-10.7202 StartY=5.36834 StartZ=0 EndX=-36.3018 EndY=-44.5439 EndZ=0
    g1: ArcOfCircle CenterX=-35.4119 CenterY=-45 CenterZ=0 NormalX=0 NormalY=0 NormalZ=1 AngleXU=0 Radius=1 StartAngle=2.66797 EndAngle=5.8242
    g2: ArcOfCircle CenterX=0 CenterY=-62.5 CenterZ=0 NormalX=0 NormalY=0 NormalZ=1 AngleXU=0 Radius=38.5 StartAngle=1.82549 EndAngle=2.68261
    g3: LineSegment StartX=-9.7 StartY=-25.242 StartZ=0 EndX=-9.7 EndY=5.12214 EndZ=0
    g4: ArcOfCircle CenterX=-10.2398 CenterY=5.12214 CenterZ=0 NormalX=0 NormalY=0 NormalZ=1 AngleXU=0 Radius=0.539788 StartAngle=-5.51e-14 EndAngle=2.66797
    g5: LineSegment [constr] StartX=-12.5 StartY=6.28057 StartZ=0 EndX=-10.7202 EndY=5.36834 EndZ=0
  constraints (14):
    c: Tangent(g0,g1) = -1.5708
    c: Tangent(g1,g2) = 1.5708
    c: Coincident(g2,g3)
    c: Parallel(g0,g-3)
    c: Vertical(g3)
    c: Distance(g-7,g3) = 2
    c: Distance(g0,g-3) = 2
    c: Coincident(g1,g-6)
    c: Coincident(g2,g-4)
    c: Tangent(g4,g0) = -1.5708
    c: Tangent(g4,g3) = -1.5708
    c: Coincident(g5,g-5)
    c: Coincident(g5,g0)
    c: Perpendicular(g-3,g5)
FEATURE [PartDesign::Pocket] Pocket022
  BaseFeature = -> Pocket018
  Direction = (0,0,-1)
  Length = 5
  Length2 = 5
  Profile = -> Sketch040
  ReferenceAxis = -> Sketch040 [N_Axis]
  Reversed = true
  Suppressed = false
  Type = 1
FEATURE [Sketcher::SketchObject] Sketch044
  ArcFitTolerance = 1e-06
  FullyConstrained = true
  MakeInternals = false
  MapMode = 5
  Placement = pos=(0,9,0) rot=(0,0.707107,0.707107;3.14159rad)
  sketch-geometry (8):
    g0: LineSegment StartX=-4.625 StartY=5 StartZ=0 EndX=-2.96 EndY=7.22 EndZ=0
    g1: LineSegment StartX=2.96 StartY=7.22 StartZ=0 EndX=4.625 EndY=5 EndZ=0
    g2: LineSegment StartX=4.625 StartY=5 StartZ=0 EndX=3.125 EndY=5 EndZ=0
    g3: LineSegment StartX=3.125 StartY=5 StartZ=0 EndX=2 EndY=6.5 EndZ=0
    g4: LineSegment StartX=-2 StartY=6.5 StartZ=0 EndX=-3.125 EndY=5 EndZ=0
    g5: LineSegment StartX=-3.125 StartY=5 StartZ=0 EndX=-4.625 EndY=5 EndZ=0
    g6: ArcOfCircle CenterX=2e-16 CenterY=5 CenterZ=0 NormalX=0 NormalY=0 NormalZ=1 AngleXU=0 Radius=2.5 StartAngle=0.643501 EndAngle=2.49809
    g7: ArcOfCircle CenterX=-3e-16 CenterY=5 CenterZ=0 NormalX=0 NormalY=0 NormalZ=1 AngleXU=0 Radius=3.7 StartAngle=0.643501 EndAngle=2.49809
  constraints (22):
    c: PointOnObject(g0,g-3)
    c: PointOnObject(g1,g-3)
    c: Coincident(g1,g2)
    c: PointOnObject(g2,g-3)
    c: Coincident(g2,g3)
    c: PointOnObject(g4,g-3)
    c: Coincident(g4,g5)
    c: Coincident(g5,g0)
    c: Symmetric(g4,g3,g-2)
    c: Equal(g4,g3)
    c: Equal(g0,g1)
    c: Symmetric(g1,g0,g-2)
    c: Distance(g3,g-3) = 1.5
    c: Coincident(g6,g3)
    c: Tangent(g6,g4) = -1.5708
    c: Tangent(g0,g7) = 1.5708
    c: Coincident(g1,g7)
    c: DistanceX(g5,g5) = 1.5
    c: PointOnObject(g7,g-3)
    c: Coincident(g6,g7)
    c: Parallel(g3,g1)
    c: Distance(g3,g1) = 1.2
FEATURE [Sketcher::SketchObject] Sketch045
  ArcFitTolerance = 1e-06
  FullyConstrained = true
  MakeInternals = false
  MapMode = 5
  Placement = pos=(0,0,5) rot=(0,0,1;0rad)
  sketch-geometry (1):
    g0: Circle CenterX=0 CenterY=7 CenterZ=0 NormalX=0 NormalY=0 NormalZ=1 AngleXU=0 Radius=1
  constraints (3):
    c: Diameter(g0) = 2
    c: PointOnObject(g0,g-2)
    c: Distance(g0,g-3) = 2
FEATURE [PartDesign::Groove] Groove002
  Angle = 360
  Angle2 = 60
  Axis = (-1,0,0)
  Base = (4.0252,9,5)
  BaseFeature = -> Pocket022
  Profile = -> Sketch045
  Reversed = true
  Suppressed = false
  Type = 0
FEATURE [Sketcher::SketchObject] Sketch046
  ArcFitTolerance = 1e-06
  AttachmentSupport = -> [Groove002]
  ExternalGeometry = -> [Groove002]
  FullyConstrained = true
  MakeInternals = false
  MapMode = 5
  Placement = pos=(0,6.0798,0) rot=(0,0.707107,0.707107;3.14159rad)
  sketch-geometry (6):
    g0: LineSegment StartX=6e-16 StartY=31.5 StartZ=0 EndX=6.2 EndY=31.5 EndZ=0
    g1: LineSegment StartX=6.2 StartY=31.5 StartZ=0 EndX=6.2 EndY=17.3 EndZ=0
    g2: LineSegment StartX=6.2 StartY=17.3 StartZ=0 EndX=0 EndY=23.5 EndZ=0
    g3: LineSegment StartX=6e-16 StartY=31.5 StartZ=0 EndX=6e-16 EndY=29.5 EndZ=0
    g4: LineSegment StartX=-4e-16 StartY=25.5 StartZ=0 EndX=0 EndY=23.5 EndZ=0
    g5: ArcOfCircle CenterX=0 CenterY=27.5 CenterZ=0 NormalX=0 NormalY=0 NormalZ=1 AngleXU=0 Radius=2 StartAngle=4.71239 EndAngle=7.85398
  constraints (19):
    c: PointOnObject(g0,g-2)
    c: PointOnObject(g0,g-3)
    c: Horizontal(g0)
    c: Coincident(g0,g1)
    c: PointOnObject(g1,g-3)
    c: Coincident(g1,g2)
    c: PointOnObject(g2,g-2)
    c: PointOnObject(g4,g-2)
    c: Coincident(g3,g0)
    c: Vertical(g3)
    c: Coincident(g4,g2)
    c: PointOnObject(g5,g-2)
    c: Coincident(g5,g3)
    c: Coincident(g5,g4)
    c: Equal(g3,g4)
    c: Angle(g1,g2) = 0.785398
    c: DistanceY(g-1,g5) = 27.5
    c: Radius(g5) = 2
    c: DistanceY(g3,g3) = 2
FEATURE [PartDesign::Pad] Pad019
  BaseFeature = -> Groove002
  Direction = (0,1,-2e-16)
  Length = 1.5
  Length2 = 10
  Profile = -> Sketch046
  ReferenceAxis = -> Sketch046 [N_Axis]
  Reversed = true
  Suppressed = false
  Type = 0
FEATURE [Sketcher::SketchObject] Sketch047
  ArcFitTolerance = 1e-06
  AttachmentSupport = -> [XY_Plane011]
  ExternalGeometry = -> [Pad019]
  FullyConstrained = true
  MakeInternals = false
  MapMode = 5
  sketch-geometry (5):
    g0: ArcOfCircle CenterX=-25.585 CenterY=0 CenterZ=0 NormalX=0 NormalY=0 NormalZ=1 AngleXU=0 Radius=4.5 StartAngle=1.09717 EndAngle=4.23877
    g1: Circle CenterX=-25.585 CenterY=0 CenterZ=0 NormalX=0 NormalY=0 NormalZ=1 AngleXU=0 Radius=1.75
    g2: LineSegment StartX=-27.6375 StartY=-4.00465 StartZ=0 EndX=-19.824 EndY=-8.00929 EndZ=0
    g3: LineSegment StartX=-19.824 StartY=-8.00929 StartZ=0 EndX=-15.719 EndY=0 EndZ=0
    g4: LineSegment StartX=-15.719 StartY=0 StartZ=0 EndX=-23.5324 EndY=4.00465 EndZ=0
  constraints (13):
    c: Coincident(g0,g1)
    c: Tangent(g0,g2) = -1.5708
    c: Coincident(g2,g3)
    c: PointOnObject(g3,g-3)
    c: Coincident(g3,g4)
    c: Tangent(g4,g0) = -1.5708
    c: Equal(g2,g4)
    c: PointOnObject(g2,g-3)
    c: Perpendicular(g3,g2)
    c: Diameter(g1) = 3.5
    c: Radius(g0) = 4.5
    c: PointOnObject(g0,g-1)
    c: PointOnObject(g3,g-1)
FEATURE [PartDesign::Pad] Pad020
  BaseFeature = -> Pad019
  Direction = (0,0,1)
  Length = 5
  Length2 = 10
  Profile = -> Sketch047
  ReferenceAxis = -> Sketch047 [N_Axis]
  Suppressed = false
  Type = 0
FEATURE [PartDesign::Fillet] Fillet004
  Base = -> Pad020 [Edge72]
  BaseFeature = -> Pad020
  Radius = 5
  SupportTransform = false
  Suppressed = false
  UseAllEdges = false
FEATURE [PartDesign::Mirrored] Mirrored001
  BaseFeature = -> Fillet004
  MirrorPlane = -> Sketch040 [V_Axis]
  Originals = -> [Pocket022,Pad019,Pad020,Fillet004]
  Suppressed = false
  TransformMode = 0
FEATURE [PartDesign::Body] Body006  label="Partie_fixe_d001"
  AllowCompound = false
  Group = -> [Sketch028,Pad012,Sketch029,Pocket018,Sketch040,Pocket022,Sketch044,Sketch045,Groove002,Sketch046,Pad019,Sketch047,Pad020,Fillet004,Mirrored001]
  Origin = -> Origin011
  Placement = pos=(50,-82.5,0) rot=(0,0,1;0rad)
  Tip = -> Mirrored001
COMPONENT P4 — recipe-attached ("CanMover_Enrouleur", modeled in this document).
Construction recipe (the document's own serialized feature program — sketch geometry with constraints, then the solid features built on it; lengths are millimeters unless a unit is written):

FEATURE [Sketcher::SketchObject] Sketch015
  ArcFitTolerance = 1e-06
  AttachmentSupport = -> [XZ_Plane008]
  FullyConstrained = true
  MakeInternals = false
  MapMode = 5
  Placement = pos=(0,0,0) rot=(1,0,0;1.5708rad)
  expr: Constraints[2] = 5.5
  expr: Constraints[5] = 3.4
  sketch-geometry (6):
    g0: Circle CenterX=0 CenterY=0 CenterZ=0 NormalX=0 NormalY=0 NormalZ=1 AngleXU=0 Radius=15
    g1: Circle CenterX=0 CenterY=0 CenterZ=0 NormalX=0 NormalY=0 NormalZ=1 AngleXU=0 Radius=2.75
    g2: Circle CenterX=0 CenterY=7 CenterZ=0 NormalX=0 NormalY=0 NormalZ=1 AngleXU=0 Radius=1.7
    g3: Circle CenterX=-7 CenterY=0 CenterZ=0 NormalX=0 NormalY=0 NormalZ=1 AngleXU=0 Radius=1.7
    g4: Circle CenterX=0 CenterY=-7 CenterZ=0 NormalX=0 NormalY=0 NormalZ=1 AngleXU=0 Radius=1.7
    g5: Circle CenterX=7 CenterY=0 CenterZ=0 NormalX=0 NormalY=0 NormalZ=1 AngleXU=0 Radius=1.7
  constraints (14):
    c: Diameter(g0) = 30
    c: Coincident(g0,g-1)
    c: Diameter(g1) = 5.5
    c: Coincident(g1,g0)
    c: PointOnObject(g2,g-2)
    c: Diameter(g2) = 3.4
    c: DistanceY(g-1,g2) = 7
    c: PointOnObject(g3,g-1)
    c: Symmetric(g5,g3,g0)
    c: Symmetric(g2,g4,g0)
    c: DistanceX(g3,g-1) = 7
    c: Equal(g5,g4)
    c: Equal(g4,g3)
    c: Equal(g3,g2)
FEATURE [PartDesign::Pad] Pad005
  Direction = (0,-1,2e-16)
  Length = 5
  Length2 = 10
  Placement = pos=(0,0,0) rot=(1,0,0;1.5708rad)
  Profile = -> Sketch015
  ReferenceAxis = -> Sketch015 [N_Axis]
  Suppressed = false
  Type = 0
FEATURE [Sketcher::SketchObject] Sketch016
  ArcFitTolerance = 1e-06
  AttachmentOffset = pos=(0,0,2) rot=(0,0,1;0rad)
  AttachmentSupport = -> [XZ_Plane008]
  FullyConstrained = true
  MakeInternals = false
  MapMode = 5
  Placement = pos=(0,-2,4e-16) rot=(1,0,0;1.5708rad)
  expr: Constraints[1] = 2.7 * 2
  sketch-geometry (1):
    g0: Circle CenterX=0 CenterY=7 CenterZ=0 NormalX=0 NormalY=0 NormalZ=1 AngleXU=0 Radius=2.7
  constraints (3):
    c: PointOnObject(g0,g-2)
    c: Diameter(g0) = 5.4
    c: DistanceY(g-1,g0) = 7
FEATURE [PartDesign::Pocket] Pocket011
  BaseFeature = -> Pad005
  Direction = (0,1,-2e-16)
  Length = 1
  Length2 = 5
  Placement = pos=(0,0,0) rot=(1,0,0;1.5708rad)
  Profile = -> Sketch016
  ReferenceAxis = -> Sketch016 [N_Axis]
  Reversed = true
  Suppressed = false
  Type = 1
FEATURE [PartDesign::PolarPattern] PolarPattern001
  Angle = 360
  Axis = -> Sketch016 [N_Axis]
  BaseFeature = -> Pocket011
  Mode = 0
  Occurrences = 4
  Offset = 120
  Originals = -> [Pocket011]
  Placement = pos=(0,0,0) rot=(1,0,0;1.5708rad)
  Suppressed = false
  TransformMode = 0
FEATURE [Sketcher::SketchObject] Sketch021
  ArcFitTolerance = 1e-06
  AttachmentSupport = -> [YZ_Plane008]
  ExternalGeometry = -> [PolarPattern001]
  FullyConstrained = true
  MakeInternals = false
  MapMode = 5
  Placement = pos=(0,0,0) rot=(0.57735,0.57735,0.57735;2.0944rad)
  sketch-geometry (4):
    g0: ArcOfCircle CenterX=-2.5 CenterY=16 CenterZ=0 NormalX=0 NormalY=0 NormalZ=1 AngleXU=0 Radius=1.80278 StartAngle=3.7296 EndAngle=5.69518
    g1: LineSegment [constr] StartX=-5 StartY=15 StartZ=0 EndX=3.6e-15 EndY=15 EndZ=0
    g2: LineSegment [constr] StartX=-2.5 StartY=16 StartZ=0 EndX=-2.5 EndY=15 EndZ=0
    g3: LineSegment StartX=-4 StartY=15 StartZ=0 EndX=-1 EndY=15 EndZ=0
  constraints (11):
    c: Coincident(g1,g-3)
    c: Coincident(g1,g-4)
    c: PointOnObject(g0,g1)
    c: PointOnObject(g0,g1)
    c: Coincident(g2,g0)
    c: Symmetric(g1,g1,g2)
    c: Vertical(g2)
    c: DistanceY(g2,g2) = 1
    c: Coincident(g3,g0)
    c: Coincident(g3,g0)
    c: Distance(g1,g0) = 1
FEATURE [PartDesign::Groove] Groove001
  Angle = 360
  Angle2 = 60
  Axis = (1e-16,1,-1e-16)
  Base = (0,0,0)
  BaseFeature = -> PolarPattern001
  Placement = pos=(0,0,0) rot=(1,0,0;1.5708rad)
  Profile = -> Sketch021
  ReferenceAxis = -> Y_Axis008
  Reversed = true
  Suppressed = false
  Type = 0
FEATURE [Sketcher::SketchObject] Sketch022
  ArcFitTolerance = 1e-06
  AttachmentSupport = -> [Groove001]
  FullyConstrained = true
  MakeInternals = false
  MapMode = 5
  Placement = pos=(0,-5,0) rot=(1,0,0;1.5708rad)
  sketch-geometry (4):
    g0: ArcOfCircle CenterX=0 CenterY=18 CenterZ=0 NormalX=0 NormalY=0 NormalZ=1 AngleXU=0 Radius=1 StartAngle=0 EndAngle=3.14159
    g1: LineSegment StartX=-1 StartY=18 StartZ=0 EndX=-1 EndY=10 EndZ=0
    g2: LineSegment StartX=-1 StartY=10 StartZ=0 EndX=1 EndY=10 EndZ=0
    g3: LineSegment StartX=1 StartY=10 StartZ=0 EndX=1 EndY=18 EndZ=0
  constraints (11):
    c: PointOnObject(g0,g-2)
    c: Vertical(g1)
    c: Coincident(g2,g1)
    c: Horizontal(g2)
    c: Vertical(g3)
    c: Coincident(g2,g3)
    c: DistanceY(g-1,g0) = 18
    c: Tangent(g1,g0) = -1.5708
    c: Tangent(g3,g0) = -1.5708
    c: Distance(g2,g2) = 2
    c: DistanceY(g-1,g1) = 10
FEATURE [PartDesign::Pad] Pad008
  BaseFeature = -> Groove001
  Direction = (0,-1,2e-16)
  Length = 5
  Length2 = 10
  Placement = pos=(0,0,0) rot=(1,0,0;1.5708rad)
  Profile = -> Sketch022
  ReferenceAxis = -> Sketch022 [N_Axis]
  Reversed = true
  Suppressed = false
  Type = 0
FEATURE [Sketcher::SketchObject] Sketch023
  ArcFitTolerance = 1e-06
  AttachmentSupport = -> [Pad008]
  ExternalGeometry = -> [Pad008]
  FullyConstrained = true
  MakeInternals = false
  MapMode = 5
  Placement = pos=(1,0,0) rot=(0.707107,0,0.707107;3.14159rad)
  sketch-geometry (3):
    g0: GeomPoint X=19 Y=2.5 Z=0
    g1: GeomPoint X=19 Y=0 Z=0
    g2: Circle CenterX=17 CenterY=2.5 CenterZ=0 NormalX=0 NormalY=0 NormalZ=1 AngleXU=0 Radius=0.75
  constraints (6):
    c: PointOnObject(g1,g-1)
    c: Symmetric(g1,g-3,g0)
    c: Horizontal(g2,g0)
    c: DistanceX(g2,g-3) = 2
    c: Diameter(g2) = 1.5
    c: Vertical(g0,g1)
FEATURE [PartDesign::Pocket] Pocket014
  BaseFeature = -> Pad008
  Direction = (-1,0,2e-16)
  Length = 5
  Length2 = 5
  Placement = pos=(0,0,0) rot=(1,0,0;1.5708rad)
  Profile = -> Sketch023
  ReferenceAxis = -> Sketch023 [N_Axis]
  Suppressed = false
  Type = 0
FEATURE [PartDesign::PolarPattern] PolarPattern002
  Angle = 360
  Axis = -> Sketch022 [N_Axis]
  BaseFeature = -> Pocket014
  Mode = 0
  Occurrences = 2
  Offset = 120
  Originals = -> [Pad008,Pocket014]
  Placement = pos=(0,0,0) rot=(1,0,0;1.5708rad)
  Suppressed = false
  TransformMode = 0
FEATURE [PartDesign::Body] Body004  label="devidoire"
  AllowCompound = false
  Group = -> [Sketch015,Pad005,Sketch016,Pocket011,PolarPattern001,Sketch021,Groove001,Sketch022,Pad008,Sketch023,Pocket014,PolarPattern002]
  Origin = -> Origin008
  Placement = pos=(0,-4.8,0) rot=(0,0,1;0rad)
  Tip = -> PolarPattern002
FEATURE [Sketcher::SketchObject] Sketch024
  ArcFitTolerance = 1e-06
  AttachmentSupport = -> [XZ_Plane009]
  FullyConstrained = true
  MakeInternals = false
  MapMode = 5
  Placement = pos=(0,0,0) rot=(1,0,0;1.5708rad)
  sketch-geometry (18):
    g0: LineSegment StartX=-10.15 StartY=29.65 StartZ=0 EndX=-10.15 EndY=-10.65 EndZ=0
    g1: LineSegment [constr] StartX=-10.15 StartY=-10.65 StartZ=0 EndX=10.15 EndY=-10.65 EndZ=0
    g2: LineSegment [constr] StartX=10.15 StartY=-10.65 StartZ=0 EndX=10.15 EndY=29.65 EndZ=0
    g3: LineSegment [constr] StartX=10.15 StartY=29.65 StartZ=0 EndX=-10.15 EndY=29.65 EndZ=0
    g4: LineSegment StartX=-14.85 StartY=37 StartZ=0 EndX=-14.85 EndY=-18 EndZ=0
    g5: LineSegment [constr] StartX=-14.85 StartY=-18 StartZ=0 EndX=14.85 EndY=-18 EndZ=0
    g6: LineSegment [constr] StartX=14.85 StartY=-18 StartZ=0 EndX=14.85 EndY=37 EndZ=0
    g7: LineSegment [constr] StartX=14.85 StartY=37 StartZ=0 EndX=-14.85 EndY=37 EndZ=0
    g8: GeomPoint X=-10.15 Y=9.5 Z=0
    g9: GeomPoint X=-14.85 Y=9.5 Z=0
    g10: LineSegment StartX=-14.85 StartY=37 StartZ=0 EndX=0 EndY=37 EndZ=0
    g11: LineSegment StartX=0 StartY=37 StartZ=0 EndX=0 EndY=29.65 EndZ=0
    g12: LineSegment StartX=0 StartY=29.65 StartZ=0 EndX=-10.15 EndY=29.65 EndZ=0
    g13: LineSegment StartX=-10.15 StartY=-10.65 StartZ=0 EndX=0 EndY=-10.65 EndZ=0
    g14: LineSegment StartX=0 StartY=-18 StartZ=0 EndX=-14.85 EndY=-18 EndZ=0
    g15: Circle CenterX=-6 CenterY=34.45 CenterZ=0 NormalX=0 NormalY=0 NormalZ=1 AngleXU=0 Radius=2.25
    g16: Circle CenterX=-6 CenterY=-15.5 CenterZ=0 NormalX=0 NormalY=0 NormalZ=1 AngleXU=0 Radius=2.25
    g17: LineSegment StartX=0 StartY=-10.65 StartZ=0 EndX=0 EndY=-18 EndZ=0
  constraints (44):
    c: Coincident(g0,g1)
    c: Coincident(g1,g2)
    c: Coincident(g2,g3)
    c: Coincident(g3,g0)
    c: Vertical(g0)
    c: Vertical(g2)
    c: Horizontal(g1)
    c: Coincident(g4,g5)
    c: Coincident(g5,g6)
    c: Coincident(g6,g7)
    c: Coincident(g7,g4)
    c: Vertical(g4)
    c: Vertical(g6)
    c: Horizontal(g5)
    c: DistanceX(g7,g7) = 29.7
    c: Symmetric(g4,g6,g-2)
    c: Symmetric(g0,g2,g-2)
    c: DistanceX(g3,g3) = 20.3
    c: DistanceY(g0,g0) = 40.3
    c: Symmetric(g0,g0,g8)
    c: DistanceY(g-1,g8) = 9.5
    c: Symmetric(g4,g4,g9)
    c: Horizontal(g9,g8)
    c: DistanceY(g4,g4) = 55
    c: Coincident(g10,g4)
    c: PointOnObject(g10,g-2)
    c: Coincident(g11,g10)
    c: PointOnObject(g11,g-2)
    c: Coincident(g12,g11)
    c: Horizontal(g12)
    c: Coincident(g13,g0)
    c: Symmetric(g1,g1,g13)
    c: Symmetric(g5,g5,g14)
    c: Coincident(g14,g4)
    c: Horizontal(g10)
    c: Coincident(g0,g12)
    c: Diameter(g15) = 4.5
    c: DistanceY(g-1,g15) = 34.45
    c: DistanceX(g15,g-1) = 6
    c: Vertical(g16,g15)
    c: Equal(g15,g16)
    c: DistanceY(g16,g-1) = 15.5
    c: Coincident(g17,g13)
    c: Coincident(g17,g14)
FEATURE [PartDesign::Pad] Pad009
  Direction = (0,-1,2e-16)
  Length = 10
  Length2 = 10
  Placement = pos=(0,0,0) rot=(1,0,0;1.5708rad)
  Profile = -> Sketch024
  ReferenceAxis = -> Sketch024 [N_Axis]
  Reversed = true
  Suppressed = false
  Type = 0
FEATURE [Sketcher::SketchObject] Sketch025
  ArcFitTolerance = 1e-06
  AttachmentSupport = -> [Pad009]
  ExternalGeometry = -> [Pad009]
  FullyConstrained = true
  MakeInternals = false
  MapMode = 5
  Placement = pos=(-14.85,0,0) rot=(0.707107,0,-0.707107;3.14159rad)
  sketch-geometry (4):
    g0: LineSegment StartX=4.15 StartY=0 StartZ=0 EndX=4.15 EndY=-4 EndZ=0
    g1: LineSegment StartX=4.15 StartY=-4 StartZ=0 EndX=8.85 EndY=-4 EndZ=0
    g2: LineSegment StartX=8.85 StartY=-4 StartZ=0 EndX=8.85 EndY=0 EndZ=0
    g3: LineSegment StartX=8.85 StartY=0 StartZ=0 EndX=4.15 EndY=0 EndZ=0
  constraints (12):
    c: Coincident(g0,g1)
    c: Coincident(g1,g2)
    c: Coincident(g2,g3)
    c: Coincident(g3,g0)
    c: Vertical(g0)
    c: Vertical(g2)
    c: Horizontal(g1)
    c: Horizontal(g3)
    c: PointOnObject(g0,g-1)
    c: DistanceX(g3,g3) = 4.7
    c: DistanceY(g2,g2) = 4
    c: DistanceX(g2,g-3) = 9.15
FEATURE [PartDesign::Pad] Pad010
  BaseFeature = -> Pad009
  Direction = (-1,0,-2e-16)
  Length = 31
  Length2 = 10
  Placement = pos=(0,0,0) rot=(1,0,0;1.5708rad)
  Profile = -> Sketch025
  ReferenceAxis = -> Sketch025 [N_Axis]
  Suppressed = false
  Type = 0
FEATURE [Sketcher::SketchObject] Sketch026
  ArcFitTolerance = 1e-06
  AttachmentSupport = -> [Pad010]
  ExternalGeometry = -> [Pad010]
  FullyConstrained = true
  MakeInternals = false
  MapMode = 5
  Placement = pos=(0,4,-9e-16) rot=(-1,0,0;1.5708rad)
  sketch-geometry (4):
    g0: LineSegment StartX=-45.85 StartY=8.85 StartZ=0 EndX=-45.85 EndY=4.15 EndZ=0
    g1: LineSegment StartX=-45.85 StartY=4.15 StartZ=0 EndX=-36.15 EndY=4.15 EndZ=0
    g2: LineSegment StartX=-36.15 StartY=4.15 StartZ=0 EndX=-36.15 EndY=8.85 EndZ=0
    g3: LineSegment StartX=-36.15 StartY=8.85 StartZ=0 EndX=-45.85 EndY=8.85 EndZ=0
  constraints (10):
    c: Coincident(g0,g1)
    c: Coincident(g1,g2)
    c: Coincident(g2,g3)
    c: Coincident(g3,g0)
    c: Vertical(g2)
    c: Horizontal(g1)
    c: Horizontal(g3)
    c: Coincident(g0,g-3)
    c: Coincident(g0,g-3)
    c: DistanceX(g3,g3) = 9.7
FEATURE [PartDesign::Pad] Pad011
  BaseFeature = -> Pad010
  Direction = (0,1,2e-16)
  Length = 5
  Length2 = 10
  Placement = pos=(0,0,0) rot=(1,0,0;1.5708rad)
  Profile = -> Sketch026
  ReferenceAxis = -> Sketch026 [N_Axis]
  Suppressed = false
  Type = 0
FEATURE [Sketcher::SketchObject] Sketch027
  ArcFitTolerance = 1e-06
  AttachmentSupport = -> [Pad011]
  ExternalGeometry = -> [Pad011]
  FullyConstrained = true
  MakeInternals = false
  MapMode = 5
  Placement = pos=(0,10,0) rot=(-1,0,0;1.5708rad)
  sketch-geometry (8):
    g0: LineSegment StartX=-14.85 StartY=18 StartZ=0 EndX=-14.85 EndY=10.65 EndZ=0
    g1: LineSegment StartX=-14.85 StartY=10.65 StartZ=0 EndX=0 EndY=10.65 EndZ=0
    g2: LineSegment StartX=0 StartY=10.65 StartZ=0 EndX=0 EndY=18 EndZ=0
    g3: LineSegment StartX=0 StartY=18 StartZ=0 EndX=-14.85 EndY=18 EndZ=0
    g4: LineSegment StartX=-14.85 StartY=-37 StartZ=0 EndX=0 EndY=-37 EndZ=0
    g5: LineSegment StartX=0 StartY=-37 StartZ=0 EndX=0 EndY=-29.65 EndZ=0
    g6: LineSegment StartX=0 StartY=-29.65 StartZ=0 EndX=-14.85 EndY=-29.65 EndZ=0
    g7: LineSegment StartX=-14.85 StartY=-29.65 StartZ=0 EndX=-14.85 EndY=-37 EndZ=0
  constraints (21):
    c: Coincident(g0,g1)
    c: Coincident(g1,g2)
    c: Coincident(g2,g3)
    c: Coincident(g3,g0)
    c: Vertical(g0)
    c: Vertical(g2)
    c: Horizontal(g1)
    c: Horizontal(g3)
    c: Coincident(g0,g-3)
    c: PointOnObject(g1,g-2)
    c: PointOnObject(g-4,g1)
    c: Coincident(g4,g5)
    c: Coincident(g5,g6)
    c: Coincident(g6,g7)
    c: Coincident(g7,g4)
    c: Horizontal(g4)
    c: Horizontal(g6)
    c: Vertical(g5)
    c: Vertical(g7)
    c: Coincident(g4,g-6)
    c: Coincident(g5,g-5)
FEATURE [PartDesign::Pocket] Pocket015
  BaseFeature = -> Pad011
  Direction = (0,-1,-2e-16)
  Length = 7
  Length2 = 5
  Placement = pos=(0,0,0) rot=(1,0,0;1.5708rad)
  Profile = -> Sketch027
  ReferenceAxis = -> Sketch027 [N_Axis]
  Suppressed = false
  Type = 0
FEATURE [PartDesign::Pocket] Pocket016
  BaseFeature = -> Pocket015
  Direction = (0,-2e-16,-1)
  Length = 1
  Length2 = 5
  Placement = pos=(0,0,0) rot=(1,0,0;1.5708rad)
  Profile = -> Pocket015 [Face1]
  Suppressed = false
  Type = 0
FEATURE [PartDesign::Pocket] Pocket017
  BaseFeature = -> Pocket016
  Direction = (0,2e-16,1)
  Length = 1
  Length2 = 5
  Placement = pos=(0,0,0) rot=(1,0,0;1.5708rad)
  Profile = -> Pocket016 [Face4]
  Suppressed = false
  Type = 0
FEATURE [PartDesign::Fillet] Fillet003
  Base = -> Pocket017 [Edge17]
  BaseFeature = -> Pocket017
  Placement = pos=(0,0,0) rot=(1,0,0;1.5708rad)
  Radius = 12
  SupportTransform = false
  Suppressed = false
  UseAllEdges = false
FEATURE [PartDesign::Chamfer] Chamfer001
  Angle = 45
  Base = -> Fillet003 [Edge24]
  BaseFeature = -> Fillet003
  ChamferType = 1
  FlipDirection = false
  Placement = pos=(0,0,0) rot=(1,0,0;1.5708rad)
  Size = 1.7
  Size2 = 10
  SupportTransform = false
  Suppressed = false
  UseAllEdges = false
FEATURE [PartDesign::Mirrored] Mirrored
  BaseFeature = -> Chamfer001
  MirrorPlane = -> YZ_Plane009
  Placement = pos=(0,0,0) rot=(1,0,0;1.5708rad)
  Suppressed = false
  TransformMode = 1
FEATURE [PartDesign::Body] Body005  label="support_servo"
  AllowCompound = false
  Group = -> [Sketch024,Pad009,Sketch025,Pad010,Sketch026,Pad011,Sketch027,Pocket015,Pocket016,Pocket017,Fillet003,Chamfer001,Mirrored]
  Origin = -> Origin009
  Placement = pos=(0,13.9,0) rot=(0,0,1;0rad)
  Tip = -> Mirrored
FEATURE [Sketcher::SketchObject] Sketch039
  ArcFitTolerance = 1e-06
  AttachmentSupport = -> [XZ_Plane016]
  FullyConstrained = true
  MakeInternals = false
  MapMode = 5
  Placement = pos=(0,0,0) rot=(1,0,0;1.5708rad)
  expr: Constraints[8] = 20.3 mm / 2
  sketch-geometry (10):
    g0: LineSegment StartX=0 StartY=-10.65 StartZ=0 EndX=10.15 EndY=-10.65 EndZ=0
    g1: LineSegment StartX=10.15 StartY=-10.65 StartZ=0 EndX=10.15 EndY=29.65 EndZ=0
    g2: LineSegment StartX=10.15 StartY=29.65 StartZ=0 EndX=0 EndY=29.65 EndZ=0
    g3: GeomPoint X=0 Y=9.5 Z=0
    g4: LineSegment StartX=0 StartY=39.65 StartZ=0 EndX=0 EndY=29.65 EndZ=0
    g5: LineSegment StartX=0 StartY=-23.65 StartZ=0 EndX=42 EndY=-23.65 EndZ=0
    g6: LineSegment StartX=42 StartY=-3.65 StartZ=0 EndX=20 EndY=39.65 EndZ=0
    g7: LineSegment StartX=20 StartY=39.65 StartZ=0 EndX=0 EndY=39.65 EndZ=0
    g8: LineSegment StartX=0 StartY=-10.65 StartZ=0 EndX=0 EndY=-23.65 EndZ=0
    g9: LineSegment StartX=42 StartY=-3.65 StartZ=0 EndX=42 EndY=-23.65 EndZ=0
  constraints (28):
    c: Coincident(g0,g1)
    c: Coincident(g1,g2)
    c: Vertical(g1)
    c: Horizontal(g0)
    c: PointOnObject(g3,g-2)
    c: Horizontal(g2)
    c: DistanceY(g-1,g3) = 9.5
    c: DistanceY(g1,g1) = 40.3
    c: DistanceX(g2,g2) = 10.15
    c: Coincident(g6,g7)
    c: Coincident(g7,g4)
    c: Vertical(g4)
    c: Horizontal(g5)
    c: Horizontal(g7)
    c: Symmetric(g2,g0,g3)
    c: Coincident(g4,g2)
    c: Coincident(g8,g0)
    c: Coincident(g8,g5)
    c: PointOnObject(g4,g-2)
    c: Vertical(g8)
    c: DistanceY(g8,g8) = 13
    c: DistanceY(g4,g4) = 10
    c: Distance(g5,g5) = 42
    c: DistanceX(g7,g7) = 20
    c: Coincident(g9,g6)
    c: Coincident(g9,g5)
    c: Vertical(g9)
    c: DistanceY(g9,g9) = 20
FEATURE [PartDesign::Pad] Pad017
  Direction = (0,-1,2e-16)
  Length = 3
  Length2 = 10
  Placement = pos=(0,0,0) rot=(1,0,0;1.5708rad)
  Profile = -> Sketch039
  ReferenceAxis = -> Sketch039 [N_Axis]
  Suppressed = false
  Type = 0
FEATURE [Sketcher::SketchObject] Sketch041
  ArcFitTolerance = 1e-06
  AttachmentOffset = pos=(0,0,32) rot=(0,0,1;0rad)
  AttachmentSupport = -> [YZ_Plane016]
  FullyConstrained = true
  MakeInternals = false
  MapMode = 5
  Placement = pos=(32,0,0) rot=(0.57735,0.57735,0.57735;2.0944rad)
  sketch-geometry (4):
    g0: LineSegment StartX=-3 StartY=-23.65 StartZ=0 EndX=-18 EndY=-23.65 EndZ=0
    g1: LineSegment StartX=-18 StartY=-23.65 StartZ=0 EndX=-18 EndY=-21.65 EndZ=0
    g2: ArcOfCircle CenterX=-18 CenterY=-6.65 CenterZ=0 NormalX=0 NormalY=0 NormalZ=1 AngleXU=0 Radius=15 StartAngle=4.71239 EndAngle=6.28319
    g3: LineSegment StartX=-3 StartY=-6.64997 StartZ=0 EndX=-3 EndY=-23.65 EndZ=0
  constraints (11):
    c: Horizontal(g0)
    c: Coincident(g0,g1)
    c: Vertical(g1)
    c: Perpendicular(g1,g2) = 4.71239
    c: Coincident(g2,g3)
    c: Coincident(g3,g0)
    c: Vertical(g3)
    c: DistanceY(g1,g1) = 2
    c: Coincident(g0,g-3)
    c: DistanceX(g0,g0) = 15
    c: Radius(g2) = 15
FEATURE [PartDesign::Pad] Pad018
  BaseFeature = -> Pad017
  Direction = (1,0,0)
  Length = 10
  Length2 = 10
  Placement = pos=(0,0,0) rot=(1,0,0;1.5708rad)
  Profile = -> Sketch041
  ReferenceAxis = -> Sketch041 [N_Axis]
  Suppressed = false
  Type = 0
FEATURE [Sketcher::SketchObject] Sketch042
  ArcFitTolerance = 1e-06
  AttachmentOffset = pos=(0,0,-10) rot=(0,0,1;0rad)
  AttachmentSupport = -> [XY_Plane016]
  ExternalGeometry = -> [Pad018]
  FullyConstrained = true
  MakeInternals = false
  MapMode = 5
  Placement = pos=(0,0,-10) rot=(0,0,1;0rad)
  sketch-geometry (3):
    g0: Circle CenterX=37 CenterY=-12.7 CenterZ=0 NormalX=0 NormalY=0 NormalZ=1 AngleXU=0 Radius=3
    g1: Circle CenterX=37 CenterY=-12.7 CenterZ=0 NormalX=0 NormalY=0 NormalZ=1 AngleXU=0 Radius=1.75
    g2: LineSegment [constr] StartX=37 StartY=-12.7 StartZ=0 EndX=37 EndY=-18 EndZ=0
  constraints (7):
    c: Coincident(g1,g0)
    c: Diameter(g1) = 3.5
    c: Diameter(g0) = 6
    c: Coincident(g2,g0)
    c: Symmetric(g-3,g-3,g2)
    c: Vertical(g2)
    c: DistanceY(g2,g2) = 5.3
FEATURE [PartDesign::Pocket] Pocket023
  BaseFeature = -> Pad018
  Direction = (0,0,-1)
  Length = 5
  Length2 = 5
  Placement = pos=(0,0,0) rot=(1,0,0;1.5708rad)
  Profile = -> Sketch042 [Edge2]
  ReferenceAxis = -> Sketch042 [N_Axis]
  Suppressed = false
  Type = 1
FEATURE [PartDesign::Pocket] Pocket024
  BaseFeature = -> Pocket023
  Direction = (0,0,-1)
  Length = 11.5
  Length2 = 5
  Placement = pos=(0,0,0) rot=(1,0,0;1.5708rad)
  Profile = -> Sketch042 [Edge1]
  ReferenceAxis = -> Sketch042 [N_Axis]
  Suppressed = false
  Type = 0
FEATURE [PartDesign::Body] Body009  label="support_devidoire"
  AllowCompound = false
  Group = -> [Sketch039,Pad017,Sketch041,Pad018,Sketch042,Pocket023,Pocket024]
  Origin = -> Origin016
  Placement = pos=(0,41.5,0) rot=(0,0,1;0rad)
  Tip = -> Pocket024
COMPONENT P5 — recipe-attached ("CanMover_Enrouleur001", modeled in this document).
Construction recipe (the document's own serialized feature program — sketch geometry with constraints, then the solid features built on it; lengths are millimeters unless a unit is written):

FEATURE [Sketcher::SketchObject] Sketch055
  ArcFitTolerance = 1e-06
  AttachmentSupport = -> [XZ_Plane021]
  FullyConstrained = true
  MakeInternals = false
  MapMode = 5
  Placement = pos=(0,0,0) rot=(1,0,0;1.5708rad)
  sketch-geometry (18):
    g0: LineSegment StartX=-10.15 StartY=29.65 StartZ=0 EndX=-10.15 EndY=-10.65 EndZ=0
    g1: LineSegment [constr] StartX=-10.15 StartY=-10.65 StartZ=0 EndX=10.15 EndY=-10.65 EndZ=0
    g2: LineSegment [constr] StartX=10.15 StartY=-10.65 StartZ=0 EndX=10.15 EndY=29.65 EndZ=0
    g3: LineSegment [constr] StartX=10.15 StartY=29.65 StartZ=0 EndX=-10.15 EndY=29.65 EndZ=0
    g4: LineSegment StartX=-14.85 StartY=37 StartZ=0 EndX=-14.85 EndY=-18 EndZ=0
    g5: LineSegment [constr] StartX=-14.85 StartY=-18 StartZ=0 EndX=14.85 EndY=-18 EndZ=0
    g6: LineSegment [constr] StartX=14.85 StartY=-18 StartZ=0 EndX=14.85 EndY=37 EndZ=0
    g7: LineSegment [constr] StartX=14.85 StartY=37 StartZ=0 EndX=-14.85 EndY=37 EndZ=0
    g8: GeomPoint X=-10.15 Y=9.5 Z=0
    g9: GeomPoint X=-14.85 Y=9.5 Z=0
    g10: LineSegment StartX=-14.85 StartY=37 StartZ=0 EndX=0 EndY=37 EndZ=0
    g11: LineSegment StartX=0 StartY=37 StartZ=0 EndX=0 EndY=29.65 EndZ=0
    g12: LineSegment StartX=0 StartY=29.65 StartZ=0 EndX=-10.15 EndY=29.65 EndZ=0
    g13: LineSegment StartX=-10.15 StartY=-10.65 StartZ=0 EndX=0 EndY=-10.65 EndZ=0
    g14: LineSegment StartX=0 StartY=-18 StartZ=0 EndX=-14.85 EndY=-18 EndZ=0
    g15: Circle CenterX=-6 CenterY=34.45 CenterZ=0 NormalX=0 NormalY=0 NormalZ=1 AngleXU=0 Radius=2.25
    g16: Circle CenterX=-6 CenterY=-15.5 CenterZ=0 NormalX=0 NormalY=0 NormalZ=1 AngleXU=0 Radius=2.25
    g17: LineSegment StartX=0 StartY=-10.65 StartZ=0 EndX=0 EndY=-18 EndZ=0
  constraints (44):
    c: Coincident(g0,g1)
    c: Coincident(g1,g2)
    c: Coincident(g2,g3)
    c: Coincident(g3,g0)
    c: Vertical(g0)
    c: Vertical(g2)
    c: Horizontal(g1)
    c: Coincident(g4,g5)
    c: Coincident(g5,g6)
    c: Coincident(g6,g7)
    c: Coincident(g7,g4)
    c: Vertical(g4)
    c: Vertical(g6)
    c: Horizontal(g5)
    c: DistanceX(g7,g7) = 29.7
    c: Symmetric(g4,g6,g-2)
    c: Symmetric(g0,g2,g-2)
    c: DistanceX(g3,g3) = 20.3
    c: DistanceY(g0,g0) = 40.3
    c: Symmetric(g0,g0,g8)
    c: DistanceY(g-1,g8) = 9.5
    c: Symmetric(g4,g4,g9)
    c: Horizontal(g9,g8)
    c: DistanceY(g4,g4) = 55
    c: Coincident(g10,g4)
    c: PointOnObject(g10,g-2)
    c: Coincident(g11,g10)
    c: PointOnObject(g11,g-2)
    c: Coincident(g12,g11)
    c: Horizontal(g12)
    c: Coincident(g13,g0)
    c: Symmetric(g1,g1,g13)
    c: Symmetric(g5,g5,g14)
    c: Coincident(g14,g4)
    c: Horizontal(g10)
    c: Coincident(g0,g12)
    c: Diameter(g15) = 4.5
    c: DistanceY(g-1,g15) = 34.45
    c: DistanceX(g15,g-1) = 6
    c: Vertical(g16,g15)
    c: Equal(g15,g16)
    c: DistanceY(g16,g-1) = 15.5
    c: Coincident(g17,g13)
    c: Coincident(g17,g14)
FEATURE [PartDesign::Pad] Pad023
  Direction = (0,-1,2e-16)
  Length = 10
  Length2 = 10
  Placement = pos=(0,0,0) rot=(1,0,0;1.5708rad)
  Profile = -> Sketch055
  ReferenceAxis = -> Sketch055 [N_Axis]
  Reversed = true
  Suppressed = false
  Type = 0
FEATURE [Sketcher::SketchObject] Sketch056
  ArcFitTolerance = 1e-06
  AttachmentSupport = -> [Pad023]
  ExternalGeometry = -> [Pad023]
  FullyConstrained = true
  MakeInternals = false
  MapMode = 5
  Placement = pos=(-14.85,0,0) rot=(0.707107,0,-0.707107;3.14159rad)
  sketch-geometry (4):
    g0: LineSegment StartX=4.15 StartY=0 StartZ=0 EndX=4.15 EndY=-4 EndZ=0
    g1: LineSegment StartX=4.15 StartY=-4 StartZ=0 EndX=8.85 EndY=-4 EndZ=0
    g2: LineSegment StartX=8.85 StartY=-4 StartZ=0 EndX=8.85 EndY=0 EndZ=0
    g3: LineSegment StartX=8.85 StartY=0 StartZ=0 EndX=4.15 EndY=0 EndZ=0
  constraints (12):
    c: Coincident(g0,g1)
    c: Coincident(g1,g2)
    c: Coincident(g2,g3)
    c: Coincident(g3,g0)
    c: Vertical(g0)
    c: Vertical(g2)
    c: Horizontal(g1)
    c: Horizontal(g3)
    c: PointOnObject(g0,g-1)
    c: DistanceX(g3,g3) = 4.7
    c: DistanceY(g2,g2) = 4
    c: DistanceX(g2,g-3) = 9.15
FEATURE [PartDesign::Pad] Pad024
  BaseFeature = -> Pad023
  Direction = (-1,0,-2e-16)
  Length = 31
  Length2 = 10
  Placement = pos=(0,0,0) rot=(1,0,0;1.5708rad)
  Profile = -> Sketch056
  ReferenceAxis = -> Sketch056 [N_Axis]
  Suppressed = false
  Type = 0
FEATURE [Sketcher::SketchObject] Sketch057
  ArcFitTolerance = 1e-06
  AttachmentSupport = -> [Pad024]
  ExternalGeometry = -> [Pad024]
  FullyConstrained = true
  MakeInternals = false
  MapMode = 5
  Placement = pos=(0,4,-9e-16) rot=(-1,0,0;1.5708rad)
  sketch-geometry (4):
    g0: LineSegment StartX=-45.85 StartY=8.85 StartZ=0 EndX=-45.85 EndY=4.15 EndZ=0
    g1: LineSegment StartX=-45.85 StartY=4.15 StartZ=0 EndX=-36.15 EndY=4.15 EndZ=0
    g2: LineSegment StartX=-36.15 StartY=4.15 StartZ=0 EndX=-36.15 EndY=8.85 EndZ=0
    g3: LineSegment StartX=-36.15 StartY=8.85 StartZ=0 EndX=-45.85 EndY=8.85 EndZ=0
  constraints (10):
    c: Coincident(g0,g1)
    c: Coincident(g1,g2)
    c: Coincident(g2,g3)
    c: Coincident(g3,g0)
    c: Vertical(g2)
    c: Horizontal(g1)
    c: Horizontal(g3)
    c: Coincident(g0,g-3)
    c: Coincident(g0,g-3)
    c: DistanceX(g3,g3) = 9.7
FEATURE [PartDesign::Pad] Pad025
  BaseFeature = -> Pad024
  Direction = (0,1,2e-16)
  Length = 5
  Length2 = 10
  Placement = pos=(0,0,0) rot=(1,0,0;1.5708rad)
  Profile = -> Sketch057
  ReferenceAxis = -> Sketch057 [N_Axis]
  Suppressed = false
  Type = 0
FEATURE [Sketcher::SketchObject] Sketch058
  ArcFitTolerance = 1e-06
  AttachmentSupport = -> [Pad025]
  ExternalGeometry = -> [Pad025]
  FullyConstrained = true
  MakeInternals = false
  MapMode = 5
  Placement = pos=(0,10,0) rot=(-1,0,0;1.5708rad)
  sketch-geometry (8):
    g0: LineSegment StartX=-14.85 StartY=18 StartZ=0 EndX=-14.85 EndY=10.65 EndZ=0
    g1: LineSegment StartX=-14.85 StartY=10.65 StartZ=0 EndX=0 EndY=10.65 EndZ=0
    g2: LineSegment StartX=0 StartY=10.65 StartZ=0 EndX=0 EndY=18 EndZ=0
    g3: LineSegment StartX=0 StartY=18 StartZ=0 EndX=-14.85 EndY=18 EndZ=0
    g4: LineSegment StartX=-14.85 StartY=-37 StartZ=0 EndX=0 EndY=-37 EndZ=0
    g5: LineSegment StartX=0 StartY=-37 StartZ=0 EndX=0 EndY=-29.65 EndZ=0
    g6: LineSegment StartX=0 StartY=-29.65 StartZ=0 EndX=-14.85 EndY=-29.65 EndZ=0
    g7: LineSegment StartX=-14.85 StartY=-29.65 StartZ=0 EndX=-14.85 EndY=-37 EndZ=0
  constraints (21):
    c: Coincident(g0,g1)
    c: Coincident(g1,g2)
    c: Coincident(g2,g3)
    c: Coincident(g3,g0)
    c: Vertical(g0)
    c: Vertical(g2)
    c: Horizontal(g1)
    c: Horizontal(g3)
    c: Coincident(g0,g-3)
    c: PointOnObject(g1,g-2)
    c: PointOnObject(g-4,g1)
    c: Coincident(g4,g5)
    c: Coincident(g5,g6)
    c: Coincident(g6,g7)
    c: Coincident(g7,g4)
    c: Horizontal(g4)
    c: Horizontal(g6)
    c: Vertical(g5)
    c: Vertical(g7)
    c: Coincident(g4,g-6)
    c: Coincident(g5,g-5)
FEATURE [PartDesign::Pocket] Pocket028
  BaseFeature = -> Pad025
  Direction = (0,-1,-2e-16)
  Length = 7
  Length2 = 5
  Placement = pos=(0,0,0) rot=(1,0,0;1.5708rad)
  Profile = -> Sketch058
  ReferenceAxis = -> Sketch058 [N_Axis]
  Suppressed = false
  Type = 0
FEATURE [PartDesign::Pocket] Pocket029
  BaseFeature = -> Pocket028
  Direction = (0,-2e-16,-1)
  Length = 1
  Length2 = 5
  Placement = pos=(0,0,0) rot=(1,0,0;1.5708rad)
  Profile = -> Pocket028 [Face1]
  Suppressed = false
  Type = 0
FEATURE [PartDesign::Pocket] Pocket030
  BaseFeature = -> Pocket029
  Direction = (0,2e-16,1)
  Length = 1
  Length2 = 5
  Placement = pos=(0,0,0) rot=(1,0,0;1.5708rad)
  Profile = -> Pocket029 [Face4]
  Suppressed = false
  Type = 0
FEATURE [PartDesign::Fillet] Fillet005
  Base = -> Pocket030 [Edge17]
  BaseFeature = -> Pocket030
  Placement = pos=(0,0,0) rot=(1,0,0;1.5708rad)
  Radius = 12
  SupportTransform = false
  Suppressed = false
  UseAllEdges = false
FEATURE [PartDesign::Chamfer] Chamfer002
  Angle = 45
  Base = -> Fillet005 [Edge24]
  BaseFeature = -> Fillet005
  ChamferType = 1
  FlipDirection = false
  Placement = pos=(0,0,0) rot=(1,0,0;1.5708rad)
  Size = 1.7
  Size2 = 10
  SupportTransform = false
  Suppressed = false
  UseAllEdges = false
FEATURE [PartDesign::Mirrored] Mirrored002
  BaseFeature = -> Chamfer002
  MirrorPlane = -> YZ_Plane021
  Placement = pos=(0,0,0) rot=(1,0,0;1.5708rad)
  Suppressed = false
  TransformMode = 1
FEATURE [PartDesign::Body] Body012  label="support_servo001"
  AllowCompound = false
  Group = -> [Sketch055,Pad023,Sketch056,Pad024,Sketch057,Pad025,Sketch058,Pocket028,Pocket029,Pocket030,Fillet005,Chamfer002,Mirrored002]
  Origin = -> Origin021
  Placement = pos=(0,13.9,0) rot=(0,0,1;0rad)
  Tip = -> Mirrored002
FEATURE [Sketcher::SketchObject] Sketch059
  ArcFitTolerance = 1e-06
  AttachmentSupport = -> [XZ_Plane022]
  FullyConstrained = true
  MakeInternals = false
  MapMode = 5
  Placement = pos=(0,0,0) rot=(1,0,0;1.5708rad)
  expr: Constraints[8] = 20.3 mm / 2
  sketch-geometry (10):
    g0: LineSegment StartX=0 StartY=-10.65 StartZ=0 EndX=10.15 EndY=-10.65 EndZ=0
    g1: LineSegment StartX=10.15 StartY=-10.65 StartZ=0 EndX=10.15 EndY=29.65 EndZ=0
    g2: LineSegment StartX=10.15 StartY=29.65 StartZ=0 EndX=0 EndY=29.65 EndZ=0
    g3: GeomPoint X=0 Y=9.5 Z=0
    g4: LineSegment StartX=0 StartY=39.65 StartZ=0 EndX=0 EndY=29.65 EndZ=0
    g5: LineSegment StartX=0 StartY=-23.65 StartZ=0 EndX=42 EndY=-23.65 EndZ=0
    g6: LineSegment StartX=42 StartY=-3.65 StartZ=0 EndX=20 EndY=39.65 EndZ=0
    g7: LineSegment StartX=20 StartY=39.65 StartZ=0 EndX=0 EndY=39.65 EndZ=0
    g8: LineSegment StartX=0 StartY=-10.65 StartZ=0 EndX=0 EndY=-23.65 EndZ=0
    g9: LineSegment StartX=42 StartY=-3.65 StartZ=0 EndX=42 EndY=-23.65 EndZ=0
  constraints (28):
    c: Coincident(g0,g1)
    c: Coincident(g1,g2)
    c: Vertical(g1)
    c: Horizontal(g0)
    c: PointOnObject(g3,g-2)
    c: Horizontal(g2)
    c: DistanceY(g-1,g3) = 9.5
    c: DistanceY(g1,g1) = 40.3
    c: DistanceX(g2,g2) = 10.15
    c: Coincident(g6,g7)
    c: Coincident(g7,g4)
    c: Vertical(g4)
    c: Horizontal(g5)
    c: Horizontal(g7)
    c: Symmetric(g2,g0,g3)
    c: Coincident(g4,g2)
    c: Coincident(g8,g0)
    c: Coincident(g8,g5)
    c: PointOnObject(g4,g-2)
    c: Vertical(g8)
    c: DistanceY(g8,g8) = 13
    c: DistanceY(g4,g4) = 10
    c: Distance(g5,g5) = 42
    c: DistanceX(g7,g7) = 20
    c: Coincident(g9,g6)
    c: Coincident(g9,g5)
    c: Vertical(g9)
    c: DistanceY(g9,g9) = 20
FEATURE [PartDesign::Pad] Pad026
  Direction = (0,-1,2e-16)
  Length = 3
  Length2 = 10
  Placement = pos=(0,0,0) rot=(1,0,0;1.5708rad)
  Profile = -> Sketch059
  ReferenceAxis = -> Sketch059 [N_Axis]
  Suppressed = false
  Type = 0
FEATURE [Sketcher::SketchObject] Sketch060
  ArcFitTolerance = 1e-06
  AttachmentOffset = pos=(0,0,32) rot=(0,0,1;0rad)
  AttachmentSupport = -> [YZ_Plane022]
  FullyConstrained = true
  MakeInternals = false
  MapMode = 5
  Placement = pos=(32,0,0) rot=(0.57735,0.57735,0.57735;2.0944rad)
  sketch-geometry (4):
    g0: LineSegment StartX=-3 StartY=-23.65 StartZ=0 EndX=-18 EndY=-23.65 EndZ=0
    g1: LineSegment StartX=-18 StartY=-23.65 StartZ=0 EndX=-18 EndY=-21.65 EndZ=0
    g2: ArcOfCircle CenterX=-18 CenterY=-6.65 CenterZ=0 NormalX=0 NormalY=0 NormalZ=1 AngleXU=0 Radius=15 StartAngle=4.71239 EndAngle=6.28319
    g3: LineSegment StartX=-3 StartY=-6.64997 StartZ=0 EndX=-3 EndY=-23.65 EndZ=0
  constraints (11):
    c: Horizontal(g0)
    c: Coincident(g0,g1)
    c: Vertical(g1)
    c: Perpendicular(g1,g2) = 4.71239
    c: Coincident(g2,g3)
    c: Coincident(g3,g0)
    c: Vertical(g3)
    c: DistanceY(g1,g1) = 2
    c: Coincident(g0,g-3)
    c: DistanceX(g0,g0) = 15
    c: Radius(g2) = 15
FEATURE [PartDesign::Pad] Pad027
  BaseFeature = -> Pad026
  Direction = (1,0,0)
  Length = 10
  Length2 = 10
  Placement = pos=(0,0,0) rot=(1,0,0;1.5708rad)
  Profile = -> Sketch060
  ReferenceAxis = -> Sketch060 [N_Axis]
  Suppressed = false
  Type = 0
FEATURE [Sketcher::SketchObject] Sketch061
  ArcFitTolerance = 1e-06
  AttachmentOffset = pos=(0,0,-10) rot=(0,0,1;0rad)
  AttachmentSupport = -> [XY_Plane022]
  ExternalGeometry = -> [Pad027]
  FullyConstrained = true
  MakeInternals = false
  MapMode = 5
  Placement = pos=(0,0,-10) rot=(0,0,1;0rad)
  sketch-geometry (3):
    g0: Circle CenterX=37 CenterY=-12.7 CenterZ=0 NormalX=0 NormalY=0 NormalZ=1 AngleXU=0 Radius=3
    g1: Circle CenterX=37 CenterY=-12.7 CenterZ=0 NormalX=0 NormalY=0 NormalZ=1 AngleXU=0 Radius=1.75
    g2: LineSegment [constr] StartX=37 StartY=-12.7 StartZ=0 EndX=37 EndY=-18 EndZ=0
  constraints (7):
    c: Coincident(g1,g0)
    c: Diameter(g1) = 3.5
    c: Diameter(g0) = 6
    c: Coincident(g2,g0)
    c: Symmetric(g-3,g-3,g2)
    c: Vertical(g2)
    c: DistanceY(g2,g2) = 5.3
FEATURE [PartDesign::Pocket] Pocket031
  BaseFeature = -> Pad027
  Direction = (0,0,-1)
  Length = 5
  Length2 = 5
  Placement = pos=(0,0,0) rot=(1,0,0;1.5708rad)
  Profile = -> Sketch061 [Edge2]
  ReferenceAxis = -> Sketch061 [N_Axis]
  Suppressed = false
  Type = 1
FEATURE [PartDesign::Pocket] Pocket032
  BaseFeature = -> Pocket031
  Direction = (0,0,-1)
  Length = 11.5
  Length2 = 5
  Placement = pos=(0,0,0) rot=(1,0,0;1.5708rad)
  Profile = -> Sketch061 [Edge1]
  ReferenceAxis = -> Sketch061 [N_Axis]
  Suppressed = false
  Type = 0
FEATURE [PartDesign::Body] Body013  label="support_devidoire001"
  AllowCompound = false
  Group = -> [Sketch059,Pad026,Sketch060,Pad027,Sketch061,Pocket031,Pocket032]
  Origin = -> Origin022
  Placement = pos=(0,41.5,0) rot=(0,0,1;0rad)
  Tip = -> Pocket032
COMPONENT P6 — recipe-attached ("clip_fil_nylon", modeled in this document).
Construction recipe (the document's own serialized feature program — sketch geometry with constraints, then the solid features built on it; lengths are millimeters unless a unit is written):

FEATURE [Sketcher::SketchObject] Sketch063
  ArcFitTolerance = 1e-06
  AttachmentSupport = -> [XZ_Plane027]
  FullyConstrained = true
  MakeInternals = false
  MapMode = 5
  Placement = pos=(0,0,0) rot=(1,0,0;1.5708rad)
  expr: Constraints[89] = .Constraints.bord + .Constraints.marge
  sketch-geometry (48):
    g0: LineSegment StartX=-7.5 StartY=0 StartZ=0 EndX=-7.5 EndY=5 EndZ=0
    g1: LineSegment StartX=-7.5 StartY=5 StartZ=0 EndX=-4.89997 EndY=5 EndZ=0
    g2: LineSegment StartX=-4.89997 StartY=5 StartZ=0 EndX=-4.5 EndY=4.14226 EndZ=0
    g3: ArcOfCircle CenterX=-4.59063 CenterY=4.1 CenterZ=0 NormalX=0 NormalY=0 NormalZ=1 AngleXU=0 Radius=0.1 StartAngle=4.71239 EndAngle=6.71952
    g4: LineSegment StartX=-4.59063 StartY=4 StartZ=0 EndX=-6.5 EndY=4 EndZ=0
    g5: LineSegment StartX=-6.5 StartY=4 StartZ=0 EndX=-6.5 EndY=1 EndZ=0
    g6: LineSegment StartX=-6.5 StartY=1 StartZ=0 EndX=-5 EndY=1 EndZ=0
    g7: LineSegment [constr] StartX=-5 StartY=1 StartZ=0 EndX=-4 EndY=3 EndZ=0
    g8: LineSegment [constr] StartX=-4 StartY=3 StartZ=0 EndX=-3 EndY=1 EndZ=0
    g9: LineSegment [constr] StartX=-3 StartY=1 StartZ=0 EndX=-2 EndY=3 EndZ=0
    g10: LineSegment [constr] StartX=-2 StartY=3 StartZ=0 EndX=-1 EndY=1 EndZ=0
    g11: LineSegment [constr] StartX=-1 StartY=1 StartZ=0 EndX=0 EndY=3 EndZ=0
    g12: LineSegment [constr] StartX=0 StartY=3 StartZ=0 EndX=1 EndY=1 EndZ=0
    g13: LineSegment [constr] StartX=1 StartY=1 StartZ=0 EndX=2 EndY=3 EndZ=0
    g14: LineSegment [constr] StartX=2 StartY=3 StartZ=0 EndX=3 EndY=1 EndZ=0
    g15: LineSegment [constr] StartX=3 StartY=1 StartZ=0 EndX=4 EndY=3 EndZ=0
    g16: LineSegment [constr] StartX=4 StartY=3 StartZ=0 EndX=5 EndY=1 EndZ=0
    g17: LineSegment StartX=5 StartY=1 StartZ=0 EndX=6.5 EndY=1 EndZ=0
    g18: LineSegment StartX=6.5 StartY=1 StartZ=0 EndX=6.5 EndY=3 EndZ=0
    g19: LineSegment StartX=6.5 StartY=3 StartZ=0 EndX=7.5 EndY=3 EndZ=0
    g20: LineSegment StartX=5.5 StartY=0 StartZ=0 EndX=-7.5 EndY=0 EndZ=0
    g21: LineSegment [constr] StartX=5 StartY=1 StartZ=0 EndX=-5 EndY=1 EndZ=0
    g22: LineSegment [constr] StartX=-5 StartY=3 StartZ=0 EndX=5 EndY=3 EndZ=0
    g23: GeomPoint [constr] X=-6.5 Y=0 Z=0
    g24: LineSegment [constr] StartX=-5 StartY=2 StartZ=0 EndX=5 EndY=2 EndZ=0
    g25: LineSegment [constr] StartX=-5 StartY=3 StartZ=0 EndX=-6.5 EndY=3 EndZ=0
    g26: LineSegment [constr] StartX=-6.5 StartY=4 StartZ=0 EndX=-7.5 EndY=4 EndZ=0
    g27: LineSegment StartX=5.5 StartY=0 StartZ=0 EndX=5.5 EndY=0.2 EndZ=0
    g28: LineSegment StartX=5.5 StartY=0.2 StartZ=0 EndX=7.5 EndY=0.2 EndZ=0
    g29: LineSegment StartX=7.5 StartY=3 StartZ=0 EndX=7.5 EndY=0.2 EndZ=0
    g30: LineSegment [constr] StartX=5 StartY=1 StartZ=0 EndX=6 EndY=3 EndZ=0
    g31: LineSegment StartX=-4.875 StartY=1 StartZ=0 EndX=-4 EndY=2.75 EndZ=0
    g32: LineSegment StartX=-4 StartY=2.75 StartZ=0 EndX=-3.125 EndY=1 EndZ=0
    g33: LineSegment StartX=-3.125 StartY=1 StartZ=0 EndX=-2.875 EndY=1 EndZ=0
    g34: LineSegment StartX=-2.875 StartY=1 StartZ=0 EndX=-2 EndY=2.75 EndZ=0
    g35: LineSegment StartX=-2 StartY=2.75 StartZ=0 EndX=-1.125 EndY=1 EndZ=0
    g36: LineSegment StartX=-1.125 StartY=1 StartZ=0 EndX=-0.875 EndY=1 EndZ=0
    g37: LineSegment StartX=-0.875 StartY=1 StartZ=0 EndX=0 EndY=2.75 EndZ=0
    g38: LineSegment StartX=0 StartY=2.75 StartZ=0 EndX=0.875 EndY=1 EndZ=0
    g39: LineSegment StartX=0.875 StartY=1 StartZ=0 EndX=1.125 EndY=1 EndZ=0
    g40: LineSegment StartX=1.125 StartY=1 StartZ=0 EndX=2 EndY=2.75 EndZ=0
    g41: LineSegment StartX=2 StartY=2.75 StartZ=0 EndX=2.875 EndY=1 EndZ=0
    g42: LineSegment StartX=2.875 StartY=1 StartZ=0 EndX=3.125 EndY=1 EndZ=0
    g43: LineSegment StartX=3.125 StartY=1 StartZ=0 EndX=4 EndY=2.75 EndZ=0
    g44: LineSegment StartX=4 StartY=2.75 StartZ=0 EndX=4.875 EndY=1 EndZ=0
    g45: LineSegment StartX=4.875 StartY=1 StartZ=0 EndX=5 EndY=1 EndZ=0
    g46: LineSegment StartX=-4.875 StartY=1 StartZ=0 EndX=-5 EndY=1 EndZ=0
    g47: LineSegment [constr] StartX=-5 StartY=2.75 StartZ=0 EndX=5 EndY=2.75 EndZ=0
  constraints (141):
    c: PointOnObject(g0,g-1)
    c: Vertical(g0)
    c: Coincident(g0,g1)
    c: Horizontal(g1)
    c: Coincident(g1,g2)
    c: Tangent(g2,g3) = 1.5708
    c: Horizontal(g4)
    c: Coincident(g4,g5)
    c: Vertical(g5)
    c: Coincident(g5,g6)
    c: Horizontal(g6)
    c: Coincident(g6,g7)
    c: Coincident(g7,g8)
    c: Coincident(g8,g9)
    c: Coincident(g9,g10)
    c: Coincident(g10,g11)
    c: Coincident(g11,g12)
    c: Coincident(g12,g13)
    c: Coincident(g13,g14)
    c: Coincident(g14,g15)
    c: Coincident(g15,g16)
    c: Coincident(g16,g17)
    c: Coincident(g17,g18)
    c: Vertical(g18)
    c: Coincident(g18,g19)
    c: Coincident(g20,g0)
    c: Horizontal(g19)
    c: Coincident(g21,g16)
    c: Coincident(g21,g6)
    c: Horizontal(g21)
    c: PointOnObject(g8,g21)
    c: PointOnObject(g10,g21)
    c: PointOnObject(g12,g21)
    c: PointOnObject(g14,g21)
    c: PointOnObject(g7,g22)
    c: PointOnObject(g9,g22)
    c: PointOnObject(g11,g22)
    c: PointOnObject(g13,g22)
    c: PointOnObject(g15,g22)
    c: Vertical(g22,g16)
    c: Vertical(g22,g6)
    c: Equal(g7,g8)
    c: Equal(g8,g9)
    c: Equal(g9,g10)
    c: Equal(g10,g11)
    c: Equal(g11,g12)
    c: Equal(g12,g13)
    c: Equal(g13,g14)
    c: Equal(g14,g15)
    c: Equal(g15,g16)
    c: Horizontal(g17)
    c: Angle(g2,g1) = 1.13446
    c: Tangent(g3,g4) = 1.5708
    c: DistanceY(g18,g18) = 2
    c: PointOnObject(g11,g-2)
    c: DistanceX(g9,g11) = 2  'espacement_triangle'
    c: PointOnObject(g23,g20)
    c: Horizontal(g18,g22)
    c: Horizontal(g22)
    c: DistanceY(g0,g5) = 1
    c: Horizontal(g24)
    c: Symmetric(g22,g6,g24)
    c: Vertical(g24,g22)
    c: Symmetric(g4,g23,g24)
    c: Coincident(g25,g22)
    c: PointOnObject(g25,g5)
    c: Horizontal(g25)
    c: Horizontal(g20)
    c: DistanceX(g19,g19) = 1  'bord'
    c: PointOnObject(g26,g0)
    c: Horizontal(g26)
    c: Coincident(g4,g26)
    c: Equal(g26,g19)
    c: Radius(g3) = 0.1
    c: DistanceX(g4,g2) = 2
    c: DistanceY(g26,g0) = 1
    c: Vertical(g27)
    c: Coincident(g28,g27)
    c: Horizontal(g28)
    c: DistanceX(g28,g28) = 2
    c: Distance(g27,g27) = 0.2
    c: Coincident(g20,g27)
    c: Coincident(g29,g19)
    c: Coincident(g29,g28)
    c: Vertical(g29)
    c: Coincident(g30,g16)
    c: PointOnObject(g30,g22)
    c: Equal(g30,g16)
    c: Distance(g18,g30) = 0.5  'marge'
    c: Distance(g25,g25) = 1.5
    c: PointOnObject(g31,g21)
    c: Coincident(g31,g32)
    c: PointOnObject(g32,g21)
    c: Coincident(g32,g33)
    c: PointOnObject(g33,g21)
    c: Coincident(g33,g34)
    c: Coincident(g34,g35)
    c: PointOnObject(g35,g21)
    c: Coincident(g35,g36)
    c: PointOnObject(g36,g21)
    c: Coincident(g36,g37)
    c: PointOnObject(g37,g-2)
    c: Coincident(g37,g38)
    c: PointOnObject(g38,g21)
    c: Coincident(g38,g39)
    c: PointOnObject(g39,g21)
    c: Coincident(g39,g40)
    c: Coincident(g40,g41)
    c: PointOnObject(g41,g21)
    c: Coincident(g41,g42)
    c: PointOnObject(g42,g21)
    c: Coincident(g42,g43)
    c: Coincident(g43,g44)
    c: PointOnObject(g44,g21)
    c: Coincident(g44,g45)
    c: Coincident(g45,g16)
    c: Coincident(g31,g46)
    c: Coincident(g46,g6)
    c: Horizontal(g47)
    c: PointOnObject(g43,g47)
    c: PointOnObject(g40,g47)
    c: PointOnObject(g37,g47)
    c: PointOnObject(g34,g47)
    c: PointOnObject(g31,g47)
    c: Equal(g44,g43)
    c: Equal(g43,g41)
    c: Equal(g41,g40)
    c: Equal(g40,g38)
    c: Equal(g38,g37)
    c: Equal(g37,g35)
    c: Equal(g35,g34)
    c: Equal(g34,g32)
    c: Equal(g32,g31)
    c: Vertical(g31,g7)
    c: Parallel(g7,g31)
    c: Distance(g31,g7) = 0.25
    c: Vertical(g34,g9)
    c: Vertical(g13,g40)
    c: Vertical(g43,g15)
    c: Vertical(g47,g22)
    c: Vertical(g47,g22)
FEATURE [PartDesign::Pad] Pad028
  Direction = (0,-1,2e-16)
  Length = 5
  Length2 = 10
  Midplane = true
  Placement = pos=(0,0,0) rot=(1,0,0;1.5708rad)
  Profile = -> Sketch063
  ReferenceAxis = -> Sketch063 [N_Axis]
  Suppressed = false
  Type = 0
FEATURE [Sketcher::SketchObject] Sketch062
  ArcFitTolerance = 1e-06
  AttachmentSupport = -> [Pad028]
  ExternalGeometry = -> [Pad028]
  FullyConstrained = true
  MakeInternals = false
  MapMode = 5
  Placement = pos=(7.5,0,0) rot=(0.707107,0,0.707107;3.14159rad)
  sketch-geometry (6):
    g0: ArcOfCircle CenterX=2 CenterY=0.75 CenterZ=0 NormalX=0 NormalY=0 NormalZ=1 AngleXU=0 Radius=0.3 StartAngle=1e-16 EndAngle=3.14159
    g1: ArcOfCircle CenterX=2 CenterY=-0.75 CenterZ=0 NormalX=0 NormalY=0 NormalZ=1 AngleXU=0 Radius=0.3 StartAngle=3.14159 EndAngle=6.28319
    g2: LineSegment StartX=2.3 StartY=0.75 StartZ=0 EndX=2.3 EndY=-0.75 EndZ=0
    g3: LineSegment StartX=1.7 StartY=0.75 StartZ=0 EndX=1.7 EndY=-0.75 EndZ=0
    g4: LineSegment [constr] StartX=1 StartY=-1e-16 StartZ=0 EndX=3 EndY=-3e-16 EndZ=0
    g5: LineSegment [constr] StartX=2 StartY=0.75 StartZ=0 EndX=2 EndY=-0.75 EndZ=0
  constraints (13):
    c: Tangent(g0,g2) = 1.5708
    c: Tangent(g0,g3) = -1.5708
    c: Tangent(g1,g2) = 1.5708
    c: Tangent(g1,g3) = -1.5708
    c: Equal(g0,g1)
    c: Symmetric(g1,g0,g-1)
    c: Symmetric(g-3,g-3,g4)
    c: Symmetric(g-4,g-4,g4)
    c: Coincident(g5,g0)
    c: Coincident(g5,g1)
    c: Symmetric(g4,g4,g5)
    c: DistanceX(g0,g0) = 0.6
    c: DistanceY(g5,g5) = 1.5
FEATURE [PartDesign::Pocket] Pocket033
  BaseFeature = -> Pad028
  Direction = (-1,0,2e-16)
  Length = 2
  Length2 = 5
  Placement = pos=(0,0,0) rot=(1,0,0;1.5708rad)
  Profile = -> Sketch062
  ReferenceAxis = -> Sketch062 [N_Axis]
  Suppressed = false
  Type = 0
FEATURE [PartDesign::Mirrored] Mirrored003
  BaseFeature = -> Pocket033
  MirrorPlane = -> YZ_Plane027
  Originals = -> [Pocket033]
  Placement = pos=(0,0,0) rot=(1,0,0;1.5708rad)
  Suppressed = false
  TransformMode = 0
FEATURE [PartDesign::Body] Body015  label="clip_fil_nylon_1"
  AllowCompound = false
  Group = -> [Sketch062,Sketch063,Pad028,Pocket033,Mirrored003]
  Origin = -> Origin027
  Tip = -> Mirrored003
FEATURE [PartDesign::SubShapeBinder] Binder
  BindCopyOnChange = 0
  BindMode = 0
  ClaimChildren = false
  Context = -> Part011 [Body016.Binder.]
  Fuse = false
  MakeFace = true
  OffsetFill = false
  OffsetIntersection = false
  OffsetJoinType = 0
  OffsetOpenResult = false
  PartialLoad = false
  Relative = true
  Support = -> [Body015,Link009]
  _Version = 2
FEATURE [Sketcher::SketchObject] Sketch064
  ArcFitTolerance = 1e-06
  AttachmentSupport = -> [YZ_Plane028]
  ExternalGeometry = -> [Binder]
  FullyConstrained = true
  MakeInternals = false
  MapMode = 5
  Placement = pos=(0,0,0) rot=(0.57735,0.57735,0.57735;2.0944rad)
  sketch-geometry (8):
    g0: LineSegment StartX=0 StartY=5.1 StartZ=0 EndX=3.6 EndY=5.1 EndZ=0
    g1: LineSegment StartX=3.6 StartY=5.1 StartZ=0 EndX=3.6 EndY=-1.1 EndZ=0
    g2: LineSegment StartX=3.6 StartY=-1.1 StartZ=0 EndX=1.6 EndY=-1.1 EndZ=0
    g3: LineSegment StartX=1.6 StartY=-1.1 StartZ=0 EndX=1.6 EndY=-0.1 EndZ=0
    g4: LineSegment StartX=1.6 StartY=-0.1 StartZ=0 EndX=2.6 EndY=-0.1 EndZ=0
    g5: LineSegment StartX=2.6 StartY=-0.1 StartZ=0 EndX=2.6 EndY=4.1 EndZ=0
    g6: LineSegment StartX=2.6 StartY=4.1 StartZ=0 EndX=0 EndY=4.1 EndZ=0
    g7: LineSegment StartX=0 StartY=5.1 StartZ=0 EndX=0 EndY=4.1 EndZ=0
  constraints (24):
    c: PointOnObject(g0,g-2)
    c: Horizontal(g0)
    c: Coincident(g0,g1)
    c: Vertical(g1)
    c: Coincident(g1,g2)
    c: Horizontal(g2)
    c: Coincident(g2,g3)
    c: Vertical(g3)
    c: Coincident(g3,g4)
    c: Horizontal(g4)
    c: Coincident(g4,g5)
    c: Vertical(g5)
    c: Coincident(g5,g6)
    c: PointOnObject(g6,g-2)
    c: Horizontal(g6)
    c: Coincident(g0,g7)
    c: Coincident(g7,g6)
    c: DistanceY(g7,g7) = 1
    c: Distance(g4,g-1) = 0.1
    c: Distance(g4,g4) = 1
    c: Equal(g3,g7)
    c: DistanceX(g5,g0) = 1
    c: DistanceX(g-3,g5) = 0.1
    c: Distance(g5,g-3) = 0.1
FEATURE [PartDesign::Pad] Pad029
  Direction = (1,0,0)
  Length = 5
  Length2 = 10
  Midplane = true
  Placement = pos=(0,0,0) rot=(1,1,1;2.0944rad)
  Profile = -> Sketch064
  ReferenceAxis = -> Sketch064 [N_Axis]
  Suppressed = false
  Type = 0
FEATURE [PartDesign::Mirrored] Mirrored004
  BaseFeature = -> Pad029
  MirrorPlane = -> Sketch064 [V_Axis]
  Originals = -> [Pad029]
  Placement = pos=(0,0,0) rot=(1,1,1;2.0944rad)
  Refine = true
  Suppressed = false
  TransformMode = 0
FEATURE [PartDesign::Body] Body016  label="clip_securisation_fil_nylon"
  AllowCompound = false
  Group = -> [Sketch064,Binder,Pad029,Mirrored004]
  Origin = -> Origin028
  Tip = -> Mirrored004
PROVENANCE & LICENSES
A FreeCAD (.FCStd) document from a public repository crawl; recipes are the document's own serialized feature recipes (and, for linked parts, companion documents' recipes).
License: as declared in the source repository (recorded in the dataset sidecar).
